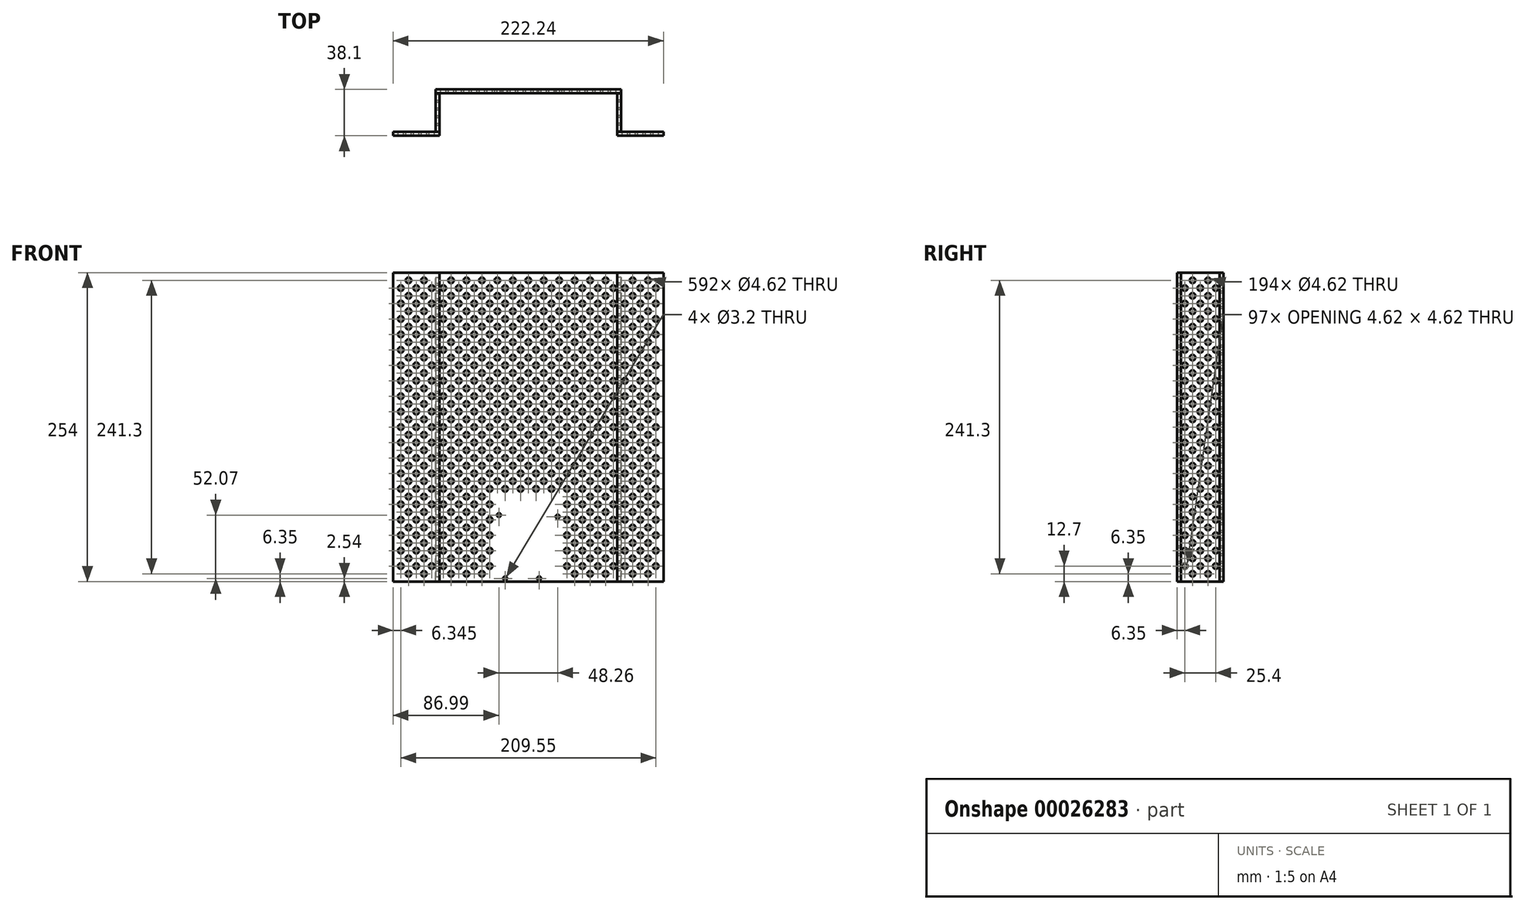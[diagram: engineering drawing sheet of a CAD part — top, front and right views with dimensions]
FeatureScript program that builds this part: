
annotation { "Feature Type Name" : "Feature", "Feature Type Description" : "" }
export const myFeature = defineFeature(function(context is Context, id is Id, definition is map)
    precondition{}
    {
        {
            var Q0;
            Q0=qCreatedBy(makeId("Front.planeOp"),FACE);
            var sketch = newSketch(context, id + "F0", { "sketchPlane" : qUnion([Q0])});
            skLineSegment(sketch, "E0.rect.bottom", {"start": v(76.2, -127) * mm, "end": v(-76.2, -127) * mm});
            skLineSegment(sketch, "E0.rect.top", {"start": v(76.2, 127) * mm, "end": v(-76.2, 127) * mm});
            skLineSegment(sketch, "E0.rect.left", {"start": v(76.2, -127) * mm, "end": v(76.2, 127) * mm});
            skLineSegment(sketch, "E0.rect.right", {"start": v(-76.2, -127) * mm, "end": v(-76.2, 127) * mm});
            skPoint(sketch, "E0.rect.middle", {"position": v(0, 0) * mm});
            skLineSegment(sketch, "E1", {"start": v(-76.2, -127) * mm, "end": v(-26.67, -127) * mm});
            skLineSegment(sketch, "E2", {"start": v(76.2, -127) * mm, "end": v(26.67, -127) * mm});
            skLineSegment(sketch, "E3.bottom", {"start": v(-26.67, -127) * mm, "end": v(26.67, -127) * mm});
            skLineSegment(sketch, "E3.top", {"start": v(-26.67, -58.42) * mm, "end": v(26.67, -58.42) * mm});
            skLineSegment(sketch, "E3.left", {"start": v(-26.67, -127) * mm, "end": v(-26.67, -58.42) * mm});
            skLineSegment(sketch, "E3.right", {"start": v(26.67, -127) * mm, "end": v(26.67, -58.42) * mm});
            skCircle(sketch, "E4", {"center": v(0, 120.65) * mm, "radius": 2.31 * mm});
            skCircle(sketch, "E5.0.1.0", {"center": v(0, 107.95) * mm, "radius": 2.31 * mm});
            skCircle(sketch, "E5.0.2.0", {"center": v(0, 95.25) * mm, "radius": 2.31 * mm});
            skCircle(sketch, "E5.0.3.0", {"center": v(0, 82.55) * mm, "radius": 2.31 * mm});
            skCircle(sketch, "E5.0.4.0", {"center": v(0, 69.85) * mm, "radius": 2.31 * mm});
            skCircle(sketch, "E5.0.5.0", {"center": v(0, 57.15) * mm, "radius": 2.31 * mm});
            skCircle(sketch, "E5.0.6.0", {"center": v(0, 44.45) * mm, "radius": 2.31 * mm});
            skCircle(sketch, "E5.0.7.0", {"center": v(0, 31.75) * mm, "radius": 2.31 * mm});
            skCircle(sketch, "E5.0.8.0", {"center": v(0, 19.05) * mm, "radius": 2.31 * mm});
            skCircle(sketch, "E5.0.9.0", {"center": v(0, 6.35) * mm, "radius": 2.31 * mm});
            skCircle(sketch, "E5.0.10.0", {"center": v(0, -6.35) * mm, "radius": 2.31 * mm});
            skCircle(sketch, "E5.0.11.0", {"center": v(0, -19.05) * mm, "radius": 2.31 * mm});
            skCircle(sketch, "E5.0.12.0", {"center": v(0, -31.75) * mm, "radius": 2.31 * mm});
            skCircle(sketch, "E5.0.13.0", {"center": v(0, -44.45) * mm, "radius": 2.31 * mm});
            skCircle(sketch, "E5.1.0.0", {"center": v(12.7, 120.65) * mm, "radius": 2.31 * mm});
            skCircle(sketch, "E5.1.1.0", {"center": v(12.7, 107.95) * mm, "radius": 2.31 * mm});
            skCircle(sketch, "E5.1.2.0", {"center": v(12.7, 95.25) * mm, "radius": 2.31 * mm});
            skCircle(sketch, "E5.1.3.0", {"center": v(12.7, 82.55) * mm, "radius": 2.31 * mm});
            skCircle(sketch, "E5.1.4.0", {"center": v(12.7, 69.85) * mm, "radius": 2.31 * mm});
            skCircle(sketch, "E5.1.5.0", {"center": v(12.7, 57.15) * mm, "radius": 2.31 * mm});
            skCircle(sketch, "E5.1.6.0", {"center": v(12.7, 44.45) * mm, "radius": 2.31 * mm});
            skCircle(sketch, "E5.1.7.0", {"center": v(12.7, 31.75) * mm, "radius": 2.31 * mm});
            skCircle(sketch, "E5.1.8.0", {"center": v(12.7, 19.05) * mm, "radius": 2.31 * mm});
            skCircle(sketch, "E5.1.9.0", {"center": v(12.7, 6.35) * mm, "radius": 2.31 * mm});
            skCircle(sketch, "E5.1.10.0", {"center": v(12.7, -6.35) * mm, "radius": 2.31 * mm});
            skCircle(sketch, "E5.1.11.0", {"center": v(12.7, -19.05) * mm, "radius": 2.31 * mm});
            skCircle(sketch, "E5.1.12.0", {"center": v(12.7, -31.75) * mm, "radius": 2.31 * mm});
            skCircle(sketch, "E5.1.13.0", {"center": v(12.7, -44.45) * mm, "radius": 2.31 * mm});
            skCircle(sketch, "E5.2.0.0", {"center": v(25.4, 120.65) * mm, "radius": 2.31 * mm});
            skCircle(sketch, "E5.2.1.0", {"center": v(25.4, 107.95) * mm, "radius": 2.31 * mm});
            skCircle(sketch, "E5.2.2.0", {"center": v(25.4, 95.25) * mm, "radius": 2.31 * mm});
            skCircle(sketch, "E5.2.3.0", {"center": v(25.4, 82.55) * mm, "radius": 2.31 * mm});
            skCircle(sketch, "E5.2.4.0", {"center": v(25.4, 69.85) * mm, "radius": 2.31 * mm});
            skCircle(sketch, "E5.2.5.0", {"center": v(25.4, 57.15) * mm, "radius": 2.31 * mm});
            skCircle(sketch, "E5.2.6.0", {"center": v(25.4, 44.45) * mm, "radius": 2.31 * mm});
            skCircle(sketch, "E5.2.7.0", {"center": v(25.4, 31.75) * mm, "radius": 2.31 * mm});
            skCircle(sketch, "E5.2.8.0", {"center": v(25.4, 19.05) * mm, "radius": 2.31 * mm});
            skCircle(sketch, "E5.2.9.0", {"center": v(25.4, 6.35) * mm, "radius": 2.31 * mm});
            skCircle(sketch, "E5.2.10.0", {"center": v(25.4, -6.35) * mm, "radius": 2.31 * mm});
            skCircle(sketch, "E5.2.11.0", {"center": v(25.4, -19.05) * mm, "radius": 2.31 * mm});
            skCircle(sketch, "E5.2.12.0", {"center": v(25.4, -31.75) * mm, "radius": 2.31 * mm});
            skCircle(sketch, "E5.2.13.0", {"center": v(25.4, -44.45) * mm, "radius": 2.31 * mm});
            skCircle(sketch, "E5.3.0.0", {"center": v(38.1, 120.65) * mm, "radius": 2.31 * mm});
            skCircle(sketch, "E5.3.1.0", {"center": v(38.1, 107.95) * mm, "radius": 2.31 * mm});
            skCircle(sketch, "E5.3.2.0", {"center": v(38.1, 95.25) * mm, "radius": 2.31 * mm});
            skCircle(sketch, "E5.3.3.0", {"center": v(38.1, 82.55) * mm, "radius": 2.31 * mm});
            skCircle(sketch, "E5.3.4.0", {"center": v(38.1, 69.85) * mm, "radius": 2.31 * mm});
            skCircle(sketch, "E5.3.5.0", {"center": v(38.1, 57.15) * mm, "radius": 2.31 * mm});
            skCircle(sketch, "E5.3.6.0", {"center": v(38.1, 44.45) * mm, "radius": 2.31 * mm});
            skCircle(sketch, "E5.3.7.0", {"center": v(38.1, 31.75) * mm, "radius": 2.31 * mm});
            skCircle(sketch, "E5.3.8.0", {"center": v(38.1, 19.05) * mm, "radius": 2.31 * mm});
            skCircle(sketch, "E5.3.9.0", {"center": v(38.1, 6.35) * mm, "radius": 2.31 * mm});
            skCircle(sketch, "E5.3.10.0", {"center": v(38.1, -6.35) * mm, "radius": 2.31 * mm});
            skCircle(sketch, "E5.3.11.0", {"center": v(38.1, -19.05) * mm, "radius": 2.31 * mm});
            skCircle(sketch, "E5.3.12.0", {"center": v(38.1, -31.75) * mm, "radius": 2.31 * mm});
            skCircle(sketch, "E5.3.13.0", {"center": v(38.1, -44.45) * mm, "radius": 2.31 * mm});
            skCircle(sketch, "E5.3.14.0", {"center": v(38.1, -57.15) * mm, "radius": 2.31 * mm});
            skCircle(sketch, "E5.3.15.0", {"center": v(38.1, -69.85) * mm, "radius": 2.31 * mm});
            skCircle(sketch, "E5.3.16.0", {"center": v(38.1, -82.55) * mm, "radius": 2.31 * mm});
            skCircle(sketch, "E5.3.17.0", {"center": v(38.1, -95.25) * mm, "radius": 2.31 * mm});
            skCircle(sketch, "E5.3.18.0", {"center": v(38.1, -107.95) * mm, "radius": 2.31 * mm});
            skCircle(sketch, "E5.3.19.0", {"center": v(38.1, -120.65) * mm, "radius": 2.31 * mm});
            skCircle(sketch, "E5.4.0.0", {"center": v(50.8, 120.65) * mm, "radius": 2.31 * mm});
            skCircle(sketch, "E5.4.1.0", {"center": v(50.8, 107.95) * mm, "radius": 2.31 * mm});
            skCircle(sketch, "E5.4.2.0", {"center": v(50.8, 95.25) * mm, "radius": 2.31 * mm});
            skCircle(sketch, "E5.4.3.0", {"center": v(50.8, 82.55) * mm, "radius": 2.31 * mm});
            skCircle(sketch, "E5.4.4.0", {"center": v(50.8, 69.85) * mm, "radius": 2.31 * mm});
            skCircle(sketch, "E5.4.5.0", {"center": v(50.8, 57.15) * mm, "radius": 2.31 * mm});
            skCircle(sketch, "E5.4.6.0", {"center": v(50.8, 44.45) * mm, "radius": 2.31 * mm});
            skCircle(sketch, "E5.4.7.0", {"center": v(50.8, 31.75) * mm, "radius": 2.31 * mm});
            skCircle(sketch, "E5.4.8.0", {"center": v(50.8, 19.05) * mm, "radius": 2.31 * mm});
            skCircle(sketch, "E5.4.9.0", {"center": v(50.8, 6.35) * mm, "radius": 2.31 * mm});
            skCircle(sketch, "E5.4.10.0", {"center": v(50.8, -6.35) * mm, "radius": 2.31 * mm});
            skCircle(sketch, "E5.4.11.0", {"center": v(50.8, -19.05) * mm, "radius": 2.31 * mm});
            skCircle(sketch, "E5.4.12.0", {"center": v(50.8, -31.75) * mm, "radius": 2.31 * mm});
            skCircle(sketch, "E5.4.13.0", {"center": v(50.8, -44.45) * mm, "radius": 2.31 * mm});
            skCircle(sketch, "E5.4.14.0", {"center": v(50.8, -57.15) * mm, "radius": 2.31 * mm});
            skCircle(sketch, "E5.4.15.0", {"center": v(50.8, -69.85) * mm, "radius": 2.31 * mm});
            skCircle(sketch, "E5.4.16.0", {"center": v(50.8, -82.55) * mm, "radius": 2.31 * mm});
            skCircle(sketch, "E5.4.17.0", {"center": v(50.8, -95.25) * mm, "radius": 2.31 * mm});
            skCircle(sketch, "E5.4.18.0", {"center": v(50.8, -107.95) * mm, "radius": 2.31 * mm});
            skCircle(sketch, "E5.4.19.0", {"center": v(50.8, -120.65) * mm, "radius": 2.31 * mm});
            skCircle(sketch, "E5.5.0.0", {"center": v(63.5, 120.65) * mm, "radius": 2.31 * mm});
            skCircle(sketch, "E5.5.1.0", {"center": v(63.5, 107.95) * mm, "radius": 2.31 * mm});
            skCircle(sketch, "E5.5.2.0", {"center": v(63.5, 95.25) * mm, "radius": 2.31 * mm});
            skCircle(sketch, "E5.5.3.0", {"center": v(63.5, 82.55) * mm, "radius": 2.31 * mm});
            skCircle(sketch, "E5.5.4.0", {"center": v(63.5, 69.85) * mm, "radius": 2.31 * mm});
            skCircle(sketch, "E5.5.5.0", {"center": v(63.5, 57.15) * mm, "radius": 2.31 * mm});
            skCircle(sketch, "E5.5.6.0", {"center": v(63.5, 44.45) * mm, "radius": 2.31 * mm});
            skCircle(sketch, "E5.5.7.0", {"center": v(63.5, 31.75) * mm, "radius": 2.31 * mm});
            skCircle(sketch, "E5.5.8.0", {"center": v(63.5, 19.05) * mm, "radius": 2.31 * mm});
            skCircle(sketch, "E5.5.9.0", {"center": v(63.5, 6.35) * mm, "radius": 2.31 * mm});
            skCircle(sketch, "E5.5.10.0", {"center": v(63.5, -6.35) * mm, "radius": 2.31 * mm});
            skCircle(sketch, "E5.5.11.0", {"center": v(63.5, -19.05) * mm, "radius": 2.31 * mm});
            skCircle(sketch, "E5.5.12.0", {"center": v(63.5, -31.75) * mm, "radius": 2.31 * mm});
            skCircle(sketch, "E5.5.13.0", {"center": v(63.5, -44.45) * mm, "radius": 2.31 * mm});
            skCircle(sketch, "E5.5.14.0", {"center": v(63.5, -57.15) * mm, "radius": 2.31 * mm});
            skCircle(sketch, "E5.5.15.0", {"center": v(63.5, -69.85) * mm, "radius": 2.31 * mm});
            skCircle(sketch, "E5.5.16.0", {"center": v(63.5, -82.55) * mm, "radius": 2.31 * mm});
            skCircle(sketch, "E5.5.17.0", {"center": v(63.5, -95.25) * mm, "radius": 2.31 * mm});
            skCircle(sketch, "E5.5.18.0", {"center": v(63.5, -107.95) * mm, "radius": 2.31 * mm});
            skCircle(sketch, "E5.5.19.0", {"center": v(63.5, -120.65) * mm, "radius": 2.31 * mm});
            skLineSegment(sketch, "E5.direction1", {"start": v(0, 120.65) * mm, "end": v(12.7, 120.65) * mm, "construction": true});
            skLineSegment(sketch, "E5.direction2", {"start": v(0, 120.65) * mm, "end": v(0, 107.95) * mm, "construction": true});
            skCircle(sketch, "E6", {"center": v(-12.7, 120.65) * mm, "radius": 2.31 * mm});
            skCircle(sketch, "E7.0.1.0", {"center": v(-12.7, 107.95) * mm, "radius": 2.31 * mm});
            skCircle(sketch, "E7.0.2.0", {"center": v(-12.7, 95.25) * mm, "radius": 2.31 * mm});
            skCircle(sketch, "E7.0.3.0", {"center": v(-12.7, 82.55) * mm, "radius": 2.31 * mm});
            skCircle(sketch, "E7.0.4.0", {"center": v(-12.7, 69.85) * mm, "radius": 2.31 * mm});
            skCircle(sketch, "E7.0.5.0", {"center": v(-12.7, 57.15) * mm, "radius": 2.31 * mm});
            skCircle(sketch, "E7.0.6.0", {"center": v(-12.7, 44.45) * mm, "radius": 2.31 * mm});
            skCircle(sketch, "E7.0.7.0", {"center": v(-12.7, 31.75) * mm, "radius": 2.31 * mm});
            skCircle(sketch, "E7.0.8.0", {"center": v(-12.7, 19.05) * mm, "radius": 2.31 * mm});
            skCircle(sketch, "E7.0.9.0", {"center": v(-12.7, 6.35) * mm, "radius": 2.31 * mm});
            skCircle(sketch, "E7.0.10.0", {"center": v(-12.7, -6.35) * mm, "radius": 2.31 * mm});
            skCircle(sketch, "E7.0.11.0", {"center": v(-12.7, -19.05) * mm, "radius": 2.31 * mm});
            skCircle(sketch, "E7.0.12.0", {"center": v(-12.7, -31.75) * mm, "radius": 2.31 * mm});
            skCircle(sketch, "E7.0.13.0", {"center": v(-12.7, -44.45) * mm, "radius": 2.31 * mm});
            skCircle(sketch, "E7.1.0.0", {"center": v(-25.4, 120.65) * mm, "radius": 2.31 * mm});
            skCircle(sketch, "E7.1.1.0", {"center": v(-25.4, 107.95) * mm, "radius": 2.31 * mm});
            skCircle(sketch, "E7.1.2.0", {"center": v(-25.4, 95.25) * mm, "radius": 2.31 * mm});
            skCircle(sketch, "E7.1.3.0", {"center": v(-25.4, 82.55) * mm, "radius": 2.31 * mm});
            skCircle(sketch, "E7.1.4.0", {"center": v(-25.4, 69.85) * mm, "radius": 2.31 * mm});
            skCircle(sketch, "E7.1.5.0", {"center": v(-25.4, 57.15) * mm, "radius": 2.31 * mm});
            skCircle(sketch, "E7.1.6.0", {"center": v(-25.4, 44.45) * mm, "radius": 2.31 * mm});
            skCircle(sketch, "E7.1.7.0", {"center": v(-25.4, 31.75) * mm, "radius": 2.31 * mm});
            skCircle(sketch, "E7.1.8.0", {"center": v(-25.4, 19.05) * mm, "radius": 2.31 * mm});
            skCircle(sketch, "E7.1.9.0", {"center": v(-25.4, 6.35) * mm, "radius": 2.31 * mm});
            skCircle(sketch, "E7.1.10.0", {"center": v(-25.4, -6.35) * mm, "radius": 2.31 * mm});
            skCircle(sketch, "E7.1.11.0", {"center": v(-25.4, -19.05) * mm, "radius": 2.31 * mm});
            skCircle(sketch, "E7.1.12.0", {"center": v(-25.4, -31.75) * mm, "radius": 2.31 * mm});
            skCircle(sketch, "E7.1.13.0", {"center": v(-25.4, -44.45) * mm, "radius": 2.31 * mm});
            skCircle(sketch, "E7.2.0.0", {"center": v(-38.1, 120.65) * mm, "radius": 2.31 * mm});
            skCircle(sketch, "E7.2.1.0", {"center": v(-38.1, 107.95) * mm, "radius": 2.31 * mm});
            skCircle(sketch, "E7.2.2.0", {"center": v(-38.1, 95.25) * mm, "radius": 2.31 * mm});
            skCircle(sketch, "E7.2.3.0", {"center": v(-38.1, 82.55) * mm, "radius": 2.31 * mm});
            skCircle(sketch, "E7.2.4.0", {"center": v(-38.1, 69.85) * mm, "radius": 2.31 * mm});
            skCircle(sketch, "E7.2.5.0", {"center": v(-38.1, 57.15) * mm, "radius": 2.31 * mm});
            skCircle(sketch, "E7.2.6.0", {"center": v(-38.1, 44.45) * mm, "radius": 2.31 * mm});
            skCircle(sketch, "E7.2.7.0", {"center": v(-38.1, 31.75) * mm, "radius": 2.31 * mm});
            skCircle(sketch, "E7.2.8.0", {"center": v(-38.1, 19.05) * mm, "radius": 2.31 * mm});
            skCircle(sketch, "E7.2.9.0", {"center": v(-38.1, 6.35) * mm, "radius": 2.31 * mm});
            skCircle(sketch, "E7.2.10.0", {"center": v(-38.1, -6.35) * mm, "radius": 2.31 * mm});
            skCircle(sketch, "E7.2.11.0", {"center": v(-38.1, -19.05) * mm, "radius": 2.31 * mm});
            skCircle(sketch, "E7.2.12.0", {"center": v(-38.1, -31.75) * mm, "radius": 2.31 * mm});
            skCircle(sketch, "E7.2.13.0", {"center": v(-38.1, -44.45) * mm, "radius": 2.31 * mm});
            skCircle(sketch, "E7.2.14.0", {"center": v(-38.1, -57.15) * mm, "radius": 2.31 * mm});
            skCircle(sketch, "E7.2.15.0", {"center": v(-38.1, -69.85) * mm, "radius": 2.31 * mm});
            skCircle(sketch, "E7.2.16.0", {"center": v(-38.1, -82.55) * mm, "radius": 2.31 * mm});
            skCircle(sketch, "E7.2.17.0", {"center": v(-38.1, -95.25) * mm, "radius": 2.31 * mm});
            skCircle(sketch, "E7.2.18.0", {"center": v(-38.1, -107.95) * mm, "radius": 2.31 * mm});
            skCircle(sketch, "E7.2.19.0", {"center": v(-38.1, -120.65) * mm, "radius": 2.31 * mm});
            skCircle(sketch, "E7.3.0.0", {"center": v(-50.8, 120.65) * mm, "radius": 2.31 * mm});
            skCircle(sketch, "E7.3.1.0", {"center": v(-50.8, 107.95) * mm, "radius": 2.31 * mm});
            skCircle(sketch, "E7.3.2.0", {"center": v(-50.8, 95.25) * mm, "radius": 2.31 * mm});
            skCircle(sketch, "E7.3.3.0", {"center": v(-50.8, 82.55) * mm, "radius": 2.31 * mm});
            skCircle(sketch, "E7.3.4.0", {"center": v(-50.8, 69.85) * mm, "radius": 2.31 * mm});
            skCircle(sketch, "E7.3.5.0", {"center": v(-50.8, 57.15) * mm, "radius": 2.31 * mm});
            skCircle(sketch, "E7.3.6.0", {"center": v(-50.8, 44.45) * mm, "radius": 2.31 * mm});
            skCircle(sketch, "E7.3.7.0", {"center": v(-50.8, 31.75) * mm, "radius": 2.31 * mm});
            skCircle(sketch, "E7.3.8.0", {"center": v(-50.8, 19.05) * mm, "radius": 2.31 * mm});
            skCircle(sketch, "E7.3.9.0", {"center": v(-50.8, 6.35) * mm, "radius": 2.31 * mm});
            skCircle(sketch, "E7.3.10.0", {"center": v(-50.8, -6.35) * mm, "radius": 2.31 * mm});
            skCircle(sketch, "E7.3.11.0", {"center": v(-50.8, -19.05) * mm, "radius": 2.31 * mm});
            skCircle(sketch, "E7.3.12.0", {"center": v(-50.8, -31.75) * mm, "radius": 2.31 * mm});
            skCircle(sketch, "E7.3.13.0", {"center": v(-50.8, -44.45) * mm, "radius": 2.31 * mm});
            skCircle(sketch, "E7.3.14.0", {"center": v(-50.8, -57.15) * mm, "radius": 2.31 * mm});
            skCircle(sketch, "E7.3.15.0", {"center": v(-50.8, -69.85) * mm, "radius": 2.31 * mm});
            skCircle(sketch, "E7.3.16.0", {"center": v(-50.8, -82.55) * mm, "radius": 2.31 * mm});
            skCircle(sketch, "E7.3.17.0", {"center": v(-50.8, -95.25) * mm, "radius": 2.31 * mm});
            skCircle(sketch, "E7.3.18.0", {"center": v(-50.8, -107.95) * mm, "radius": 2.31 * mm});
            skCircle(sketch, "E7.3.19.0", {"center": v(-50.8, -120.65) * mm, "radius": 2.31 * mm});
            skCircle(sketch, "E7.4.0.0", {"center": v(-63.5, 120.65) * mm, "radius": 2.31 * mm});
            skCircle(sketch, "E7.4.1.0", {"center": v(-63.5, 107.95) * mm, "radius": 2.31 * mm});
            skCircle(sketch, "E7.4.2.0", {"center": v(-63.5, 95.25) * mm, "radius": 2.31 * mm});
            skCircle(sketch, "E7.4.3.0", {"center": v(-63.5, 82.55) * mm, "radius": 2.31 * mm});
            skCircle(sketch, "E7.4.4.0", {"center": v(-63.5, 69.85) * mm, "radius": 2.31 * mm});
            skCircle(sketch, "E7.4.5.0", {"center": v(-63.5, 57.15) * mm, "radius": 2.31 * mm});
            skCircle(sketch, "E7.4.6.0", {"center": v(-63.5, 44.45) * mm, "radius": 2.31 * mm});
            skCircle(sketch, "E7.4.7.0", {"center": v(-63.5, 31.75) * mm, "radius": 2.31 * mm});
            skCircle(sketch, "E7.4.8.0", {"center": v(-63.5, 19.05) * mm, "radius": 2.31 * mm});
            skCircle(sketch, "E7.4.9.0", {"center": v(-63.5, 6.35) * mm, "radius": 2.31 * mm});
            skCircle(sketch, "E7.4.10.0", {"center": v(-63.5, -6.35) * mm, "radius": 2.31 * mm});
            skCircle(sketch, "E7.4.11.0", {"center": v(-63.5, -19.05) * mm, "radius": 2.31 * mm});
            skCircle(sketch, "E7.4.12.0", {"center": v(-63.5, -31.75) * mm, "radius": 2.31 * mm});
            skCircle(sketch, "E7.4.13.0", {"center": v(-63.5, -44.45) * mm, "radius": 2.31 * mm});
            skCircle(sketch, "E7.4.14.0", {"center": v(-63.5, -57.15) * mm, "radius": 2.31 * mm});
            skCircle(sketch, "E7.4.15.0", {"center": v(-63.5, -69.85) * mm, "radius": 2.31 * mm});
            skCircle(sketch, "E7.4.16.0", {"center": v(-63.5, -82.55) * mm, "radius": 2.31 * mm});
            skCircle(sketch, "E7.4.17.0", {"center": v(-63.5, -95.25) * mm, "radius": 2.31 * mm});
            skCircle(sketch, "E7.4.18.0", {"center": v(-63.5, -107.95) * mm, "radius": 2.31 * mm});
            skCircle(sketch, "E7.4.19.0", {"center": v(-63.5, -120.65) * mm, "radius": 2.31 * mm});
            skLineSegment(sketch, "E7.direction1", {"start": v(-12.7, 120.65) * mm, "end": v(-25.4, 120.65) * mm, "construction": true});
            skLineSegment(sketch, "E7.direction2", {"start": v(-12.7, 120.65) * mm, "end": v(-12.7, 107.95) * mm, "construction": true});
            skCircle(sketch, "E8", {"center": v(6.35, 114.3) * mm, "radius": 2.31 * mm});
            skCircle(sketch, "E9.0.1.0", {"center": v(6.35, 101.6) * mm, "radius": 2.31 * mm});
            skCircle(sketch, "E9.0.2.0", {"center": v(6.35, 88.9) * mm, "radius": 2.31 * mm});
            skCircle(sketch, "E9.0.3.0", {"center": v(6.35, 76.2) * mm, "radius": 2.31 * mm});
            skCircle(sketch, "E9.0.4.0", {"center": v(6.35, 63.5) * mm, "radius": 2.31 * mm});
            skCircle(sketch, "E9.0.5.0", {"center": v(6.35, 50.8) * mm, "radius": 2.31 * mm});
            skCircle(sketch, "E9.0.6.0", {"center": v(6.35, 38.1) * mm, "radius": 2.31 * mm});
            skCircle(sketch, "E9.0.7.0", {"center": v(6.35, 25.4) * mm, "radius": 2.31 * mm});
            skCircle(sketch, "E9.0.8.0", {"center": v(6.35, 12.7) * mm, "radius": 2.31 * mm});
            skCircle(sketch, "E9.0.9.0", {"center": v(6.35, 0) * mm, "radius": 2.31 * mm});
            skCircle(sketch, "E9.0.10.0", {"center": v(6.35, -12.7) * mm, "radius": 2.31 * mm});
            skCircle(sketch, "E9.0.11.0", {"center": v(6.35, -25.4) * mm, "radius": 2.31 * mm});
            skCircle(sketch, "E9.0.12.0", {"center": v(6.35, -38.1) * mm, "radius": 2.31 * mm});
            skCircle(sketch, "E9.0.13.0", {"center": v(6.35, -50.8) * mm, "radius": 2.31 * mm});
            skCircle(sketch, "E9.1.0.0", {"center": v(19.05, 114.3) * mm, "radius": 2.31 * mm});
            skCircle(sketch, "E9.1.1.0", {"center": v(19.05, 101.6) * mm, "radius": 2.31 * mm});
            skCircle(sketch, "E9.1.2.0", {"center": v(19.05, 88.9) * mm, "radius": 2.31 * mm});
            skCircle(sketch, "E9.1.3.0", {"center": v(19.05, 76.2) * mm, "radius": 2.31 * mm});
            skCircle(sketch, "E9.1.4.0", {"center": v(19.05, 63.5) * mm, "radius": 2.31 * mm});
            skCircle(sketch, "E9.1.5.0", {"center": v(19.05, 50.8) * mm, "radius": 2.31 * mm});
            skCircle(sketch, "E9.1.6.0", {"center": v(19.05, 38.1) * mm, "radius": 2.31 * mm});
            skCircle(sketch, "E9.1.7.0", {"center": v(19.05, 25.4) * mm, "radius": 2.31 * mm});
            skCircle(sketch, "E9.1.8.0", {"center": v(19.05, 12.7) * mm, "radius": 2.31 * mm});
            skCircle(sketch, "E9.1.9.0", {"center": v(19.05, 0) * mm, "radius": 2.31 * mm});
            skCircle(sketch, "E9.1.10.0", {"center": v(19.05, -12.7) * mm, "radius": 2.31 * mm});
            skCircle(sketch, "E9.1.11.0", {"center": v(19.05, -25.4) * mm, "radius": 2.31 * mm});
            skCircle(sketch, "E9.1.12.0", {"center": v(19.05, -38.1) * mm, "radius": 2.31 * mm});
            skCircle(sketch, "E9.1.13.0", {"center": v(19.05, -50.8) * mm, "radius": 2.31 * mm});
            skCircle(sketch, "E9.2.0.0", {"center": v(31.75, 114.3) * mm, "radius": 2.31 * mm});
            skCircle(sketch, "E9.2.1.0", {"center": v(31.75, 101.6) * mm, "radius": 2.31 * mm});
            skCircle(sketch, "E9.2.2.0", {"center": v(31.75, 88.9) * mm, "radius": 2.31 * mm});
            skCircle(sketch, "E9.2.3.0", {"center": v(31.75, 76.2) * mm, "radius": 2.31 * mm});
            skCircle(sketch, "E9.2.4.0", {"center": v(31.75, 63.5) * mm, "radius": 2.31 * mm});
            skCircle(sketch, "E9.2.5.0", {"center": v(31.75, 50.8) * mm, "radius": 2.31 * mm});
            skCircle(sketch, "E9.2.6.0", {"center": v(31.75, 38.1) * mm, "radius": 2.31 * mm});
            skCircle(sketch, "E9.2.7.0", {"center": v(31.75, 25.4) * mm, "radius": 2.31 * mm});
            skCircle(sketch, "E9.2.8.0", {"center": v(31.75, 12.7) * mm, "radius": 2.31 * mm});
            skCircle(sketch, "E9.2.9.0", {"center": v(31.75, 0) * mm, "radius": 2.31 * mm});
            skCircle(sketch, "E9.2.10.0", {"center": v(31.75, -12.7) * mm, "radius": 2.31 * mm});
            skCircle(sketch, "E9.2.11.0", {"center": v(31.75, -25.4) * mm, "radius": 2.31 * mm});
            skCircle(sketch, "E9.2.12.0", {"center": v(31.75, -38.1) * mm, "radius": 2.31 * mm});
            skCircle(sketch, "E9.2.13.0", {"center": v(31.75, -50.8) * mm, "radius": 2.31 * mm});
            skCircle(sketch, "E9.2.14.0", {"center": v(31.75, -63.5) * mm, "radius": 2.31 * mm});
            skCircle(sketch, "E9.2.15.0", {"center": v(31.75, -76.2) * mm, "radius": 2.31 * mm});
            skCircle(sketch, "E9.2.16.0", {"center": v(31.75, -88.9) * mm, "radius": 2.31 * mm});
            skCircle(sketch, "E9.2.17.0", {"center": v(31.75, -101.6) * mm, "radius": 2.31 * mm});
            skCircle(sketch, "E9.2.18.0", {"center": v(31.75, -114.3) * mm, "radius": 2.31 * mm});
            skCircle(sketch, "E9.3.0.0", {"center": v(44.45, 114.3) * mm, "radius": 2.31 * mm});
            skCircle(sketch, "E9.3.1.0", {"center": v(44.45, 101.6) * mm, "radius": 2.31 * mm});
            skCircle(sketch, "E9.3.2.0", {"center": v(44.45, 88.9) * mm, "radius": 2.31 * mm});
            skCircle(sketch, "E9.3.3.0", {"center": v(44.45, 76.2) * mm, "radius": 2.31 * mm});
            skCircle(sketch, "E9.3.4.0", {"center": v(44.45, 63.5) * mm, "radius": 2.31 * mm});
            skCircle(sketch, "E9.3.5.0", {"center": v(44.45, 50.8) * mm, "radius": 2.31 * mm});
            skCircle(sketch, "E9.3.6.0", {"center": v(44.45, 38.1) * mm, "radius": 2.31 * mm});
            skCircle(sketch, "E9.3.7.0", {"center": v(44.45, 25.4) * mm, "radius": 2.31 * mm});
            skCircle(sketch, "E9.3.8.0", {"center": v(44.45, 12.7) * mm, "radius": 2.31 * mm});
            skCircle(sketch, "E9.3.9.0", {"center": v(44.45, 0) * mm, "radius": 2.31 * mm});
            skCircle(sketch, "E9.3.10.0", {"center": v(44.45, -12.7) * mm, "radius": 2.31 * mm});
            skCircle(sketch, "E9.3.11.0", {"center": v(44.45, -25.4) * mm, "radius": 2.31 * mm});
            skCircle(sketch, "E9.3.12.0", {"center": v(44.45, -38.1) * mm, "radius": 2.31 * mm});
            skCircle(sketch, "E9.3.13.0", {"center": v(44.45, -50.8) * mm, "radius": 2.31 * mm});
            skCircle(sketch, "E9.3.14.0", {"center": v(44.45, -63.5) * mm, "radius": 2.31 * mm});
            skCircle(sketch, "E9.3.15.0", {"center": v(44.45, -76.2) * mm, "radius": 2.31 * mm});
            skCircle(sketch, "E9.3.16.0", {"center": v(44.45, -88.9) * mm, "radius": 2.31 * mm});
            skCircle(sketch, "E9.3.17.0", {"center": v(44.45, -101.6) * mm, "radius": 2.31 * mm});
            skCircle(sketch, "E9.3.18.0", {"center": v(44.45, -114.3) * mm, "radius": 2.31 * mm});
            skCircle(sketch, "E9.4.0.0", {"center": v(57.15, 114.3) * mm, "radius": 2.31 * mm});
            skCircle(sketch, "E9.4.1.0", {"center": v(57.15, 101.6) * mm, "radius": 2.31 * mm});
            skCircle(sketch, "E9.4.2.0", {"center": v(57.15, 88.9) * mm, "radius": 2.31 * mm});
            skCircle(sketch, "E9.4.3.0", {"center": v(57.15, 76.2) * mm, "radius": 2.31 * mm});
            skCircle(sketch, "E9.4.4.0", {"center": v(57.15, 63.5) * mm, "radius": 2.31 * mm});
            skCircle(sketch, "E9.4.5.0", {"center": v(57.15, 50.8) * mm, "radius": 2.31 * mm});
            skCircle(sketch, "E9.4.6.0", {"center": v(57.15, 38.1) * mm, "radius": 2.31 * mm});
            skCircle(sketch, "E9.4.7.0", {"center": v(57.15, 25.4) * mm, "radius": 2.31 * mm});
            skCircle(sketch, "E9.4.8.0", {"center": v(57.15, 12.7) * mm, "radius": 2.31 * mm});
            skCircle(sketch, "E9.4.9.0", {"center": v(57.15, 0) * mm, "radius": 2.31 * mm});
            skCircle(sketch, "E9.4.10.0", {"center": v(57.15, -12.7) * mm, "radius": 2.31 * mm});
            skCircle(sketch, "E9.4.11.0", {"center": v(57.15, -25.4) * mm, "radius": 2.31 * mm});
            skCircle(sketch, "E9.4.12.0", {"center": v(57.15, -38.1) * mm, "radius": 2.31 * mm});
            skCircle(sketch, "E9.4.13.0", {"center": v(57.15, -50.8) * mm, "radius": 2.31 * mm});
            skCircle(sketch, "E9.4.14.0", {"center": v(57.15, -63.5) * mm, "radius": 2.31 * mm});
            skCircle(sketch, "E9.4.15.0", {"center": v(57.15, -76.2) * mm, "radius": 2.31 * mm});
            skCircle(sketch, "E9.4.16.0", {"center": v(57.15, -88.9) * mm, "radius": 2.31 * mm});
            skCircle(sketch, "E9.4.17.0", {"center": v(57.15, -101.6) * mm, "radius": 2.31 * mm});
            skCircle(sketch, "E9.4.18.0", {"center": v(57.15, -114.3) * mm, "radius": 2.31 * mm});
            skCircle(sketch, "E9.5.0.0", {"center": v(69.85, 114.3) * mm, "radius": 2.31 * mm});
            skCircle(sketch, "E9.5.1.0", {"center": v(69.85, 101.6) * mm, "radius": 2.31 * mm});
            skCircle(sketch, "E9.5.2.0", {"center": v(69.85, 88.9) * mm, "radius": 2.31 * mm});
            skCircle(sketch, "E9.5.3.0", {"center": v(69.85, 76.2) * mm, "radius": 2.31 * mm});
            skCircle(sketch, "E9.5.4.0", {"center": v(69.85, 63.5) * mm, "radius": 2.31 * mm});
            skCircle(sketch, "E9.5.5.0", {"center": v(69.85, 50.8) * mm, "radius": 2.31 * mm});
            skCircle(sketch, "E9.5.6.0", {"center": v(69.85, 38.1) * mm, "radius": 2.31 * mm});
            skCircle(sketch, "E9.5.7.0", {"center": v(69.85, 25.4) * mm, "radius": 2.31 * mm});
            skCircle(sketch, "E9.5.8.0", {"center": v(69.85, 12.7) * mm, "radius": 2.31 * mm});
            skCircle(sketch, "E9.5.9.0", {"center": v(69.85, 0) * mm, "radius": 2.31 * mm});
            skCircle(sketch, "E9.5.10.0", {"center": v(69.85, -12.7) * mm, "radius": 2.31 * mm});
            skCircle(sketch, "E9.5.11.0", {"center": v(69.85, -25.4) * mm, "radius": 2.31 * mm});
            skCircle(sketch, "E9.5.12.0", {"center": v(69.85, -38.1) * mm, "radius": 2.31 * mm});
            skCircle(sketch, "E9.5.13.0", {"center": v(69.85, -50.8) * mm, "radius": 2.31 * mm});
            skCircle(sketch, "E9.5.14.0", {"center": v(69.85, -63.5) * mm, "radius": 2.31 * mm});
            skCircle(sketch, "E9.5.15.0", {"center": v(69.85, -76.2) * mm, "radius": 2.31 * mm});
            skCircle(sketch, "E9.5.16.0", {"center": v(69.85, -88.9) * mm, "radius": 2.31 * mm});
            skCircle(sketch, "E9.5.17.0", {"center": v(69.85, -101.6) * mm, "radius": 2.31 * mm});
            skCircle(sketch, "E9.5.18.0", {"center": v(69.85, -114.3) * mm, "radius": 2.31 * mm});
            skLineSegment(sketch, "E9.direction1", {"start": v(6.35, 114.3) * mm, "end": v(19.05, 114.3) * mm, "construction": true});
            skLineSegment(sketch, "E9.direction2", {"start": v(6.35, 114.3) * mm, "end": v(6.35, 101.6) * mm, "construction": true});
            skCircle(sketch, "E10", {"center": v(-6.35, 114.3) * mm, "radius": 2.31 * mm});
            skCircle(sketch, "E11.0.1.0", {"center": v(-6.35, 101.6) * mm, "radius": 2.31 * mm});
            skCircle(sketch, "E11.0.2.0", {"center": v(-6.35, 88.9) * mm, "radius": 2.31 * mm});
            skCircle(sketch, "E11.0.3.0", {"center": v(-6.35, 76.2) * mm, "radius": 2.31 * mm});
            skCircle(sketch, "E11.0.4.0", {"center": v(-6.35, 63.5) * mm, "radius": 2.31 * mm});
            skCircle(sketch, "E11.0.5.0", {"center": v(-6.35, 50.8) * mm, "radius": 2.31 * mm});
            skCircle(sketch, "E11.0.6.0", {"center": v(-6.35, 38.1) * mm, "radius": 2.31 * mm});
            skCircle(sketch, "E11.0.7.0", {"center": v(-6.35, 25.4) * mm, "radius": 2.31 * mm});
            skCircle(sketch, "E11.0.8.0", {"center": v(-6.35, 12.7) * mm, "radius": 2.31 * mm});
            skCircle(sketch, "E11.0.9.0", {"center": v(-6.35, 0) * mm, "radius": 2.31 * mm});
            skCircle(sketch, "E11.0.10.0", {"center": v(-6.35, -12.7) * mm, "radius": 2.31 * mm});
            skCircle(sketch, "E11.0.11.0", {"center": v(-6.35, -25.4) * mm, "radius": 2.31 * mm});
            skCircle(sketch, "E11.0.12.0", {"center": v(-6.35, -38.1) * mm, "radius": 2.31 * mm});
            skCircle(sketch, "E11.0.13.0", {"center": v(-6.35, -50.8) * mm, "radius": 2.31 * mm});
            skCircle(sketch, "E11.1.0.0", {"center": v(-19.05, 114.3) * mm, "radius": 2.31 * mm});
            skCircle(sketch, "E11.1.1.0", {"center": v(-19.05, 101.6) * mm, "radius": 2.31 * mm});
            skCircle(sketch, "E11.1.2.0", {"center": v(-19.05, 88.9) * mm, "radius": 2.31 * mm});
            skCircle(sketch, "E11.1.3.0", {"center": v(-19.05, 76.2) * mm, "radius": 2.31 * mm});
            skCircle(sketch, "E11.1.4.0", {"center": v(-19.05, 63.5) * mm, "radius": 2.31 * mm});
            skCircle(sketch, "E11.1.5.0", {"center": v(-19.05, 50.8) * mm, "radius": 2.31 * mm});
            skCircle(sketch, "E11.1.6.0", {"center": v(-19.05, 38.1) * mm, "radius": 2.31 * mm});
            skCircle(sketch, "E11.1.7.0", {"center": v(-19.05, 25.4) * mm, "radius": 2.31 * mm});
            skCircle(sketch, "E11.1.8.0", {"center": v(-19.05, 12.7) * mm, "radius": 2.31 * mm});
            skCircle(sketch, "E11.1.9.0", {"center": v(-19.05, 0) * mm, "radius": 2.31 * mm});
            skCircle(sketch, "E11.1.10.0", {"center": v(-19.05, -12.7) * mm, "radius": 2.31 * mm});
            skCircle(sketch, "E11.1.11.0", {"center": v(-19.05, -25.4) * mm, "radius": 2.31 * mm});
            skCircle(sketch, "E11.1.12.0", {"center": v(-19.05, -38.1) * mm, "radius": 2.31 * mm});
            skCircle(sketch, "E11.1.13.0", {"center": v(-19.05, -50.8) * mm, "radius": 2.31 * mm});
            skCircle(sketch, "E11.2.0.0", {"center": v(-31.75, 114.3) * mm, "radius": 2.31 * mm});
            skCircle(sketch, "E11.2.1.0", {"center": v(-31.75, 101.6) * mm, "radius": 2.31 * mm});
            skCircle(sketch, "E11.2.2.0", {"center": v(-31.75, 88.9) * mm, "radius": 2.31 * mm});
            skCircle(sketch, "E11.2.3.0", {"center": v(-31.75, 76.2) * mm, "radius": 2.31 * mm});
            skCircle(sketch, "E11.2.4.0", {"center": v(-31.75, 63.5) * mm, "radius": 2.31 * mm});
            skCircle(sketch, "E11.2.5.0", {"center": v(-31.75, 50.8) * mm, "radius": 2.31 * mm});
            skCircle(sketch, "E11.2.6.0", {"center": v(-31.75, 38.1) * mm, "radius": 2.31 * mm});
            skCircle(sketch, "E11.2.7.0", {"center": v(-31.75, 25.4) * mm, "radius": 2.31 * mm});
            skCircle(sketch, "E11.2.8.0", {"center": v(-31.75, 12.7) * mm, "radius": 2.31 * mm});
            skCircle(sketch, "E11.2.9.0", {"center": v(-31.75, 0) * mm, "radius": 2.31 * mm});
            skCircle(sketch, "E11.2.10.0", {"center": v(-31.75, -12.7) * mm, "radius": 2.31 * mm});
            skCircle(sketch, "E11.2.11.0", {"center": v(-31.75, -25.4) * mm, "radius": 2.31 * mm});
            skCircle(sketch, "E11.2.12.0", {"center": v(-31.75, -38.1) * mm, "radius": 2.31 * mm});
            skCircle(sketch, "E11.2.13.0", {"center": v(-31.75, -50.8) * mm, "radius": 2.31 * mm});
            skCircle(sketch, "E11.2.14.0", {"center": v(-31.75, -63.5) * mm, "radius": 2.31 * mm});
            skCircle(sketch, "E11.2.15.0", {"center": v(-31.75, -76.2) * mm, "radius": 2.31 * mm});
            skCircle(sketch, "E11.2.16.0", {"center": v(-31.75, -88.9) * mm, "radius": 2.31 * mm});
            skCircle(sketch, "E11.2.17.0", {"center": v(-31.75, -101.6) * mm, "radius": 2.31 * mm});
            skCircle(sketch, "E11.2.18.0", {"center": v(-31.75, -114.3) * mm, "radius": 2.31 * mm});
            skCircle(sketch, "E11.3.0.0", {"center": v(-44.45, 114.3) * mm, "radius": 2.31 * mm});
            skCircle(sketch, "E11.3.1.0", {"center": v(-44.45, 101.6) * mm, "radius": 2.31 * mm});
            skCircle(sketch, "E11.3.2.0", {"center": v(-44.45, 88.9) * mm, "radius": 2.31 * mm});
            skCircle(sketch, "E11.3.3.0", {"center": v(-44.45, 76.2) * mm, "radius": 2.31 * mm});
            skCircle(sketch, "E11.3.4.0", {"center": v(-44.45, 63.5) * mm, "radius": 2.31 * mm});
            skCircle(sketch, "E11.3.5.0", {"center": v(-44.45, 50.8) * mm, "radius": 2.31 * mm});
            skCircle(sketch, "E11.3.6.0", {"center": v(-44.45, 38.1) * mm, "radius": 2.31 * mm});
            skCircle(sketch, "E11.3.7.0", {"center": v(-44.45, 25.4) * mm, "radius": 2.31 * mm});
            skCircle(sketch, "E11.3.8.0", {"center": v(-44.45, 12.7) * mm, "radius": 2.31 * mm});
            skCircle(sketch, "E11.3.9.0", {"center": v(-44.45, 0) * mm, "radius": 2.31 * mm});
            skCircle(sketch, "E11.3.10.0", {"center": v(-44.45, -12.7) * mm, "radius": 2.31 * mm});
            skCircle(sketch, "E11.3.11.0", {"center": v(-44.45, -25.4) * mm, "radius": 2.31 * mm});
            skCircle(sketch, "E11.3.12.0", {"center": v(-44.45, -38.1) * mm, "radius": 2.31 * mm});
            skCircle(sketch, "E11.3.13.0", {"center": v(-44.45, -50.8) * mm, "radius": 2.31 * mm});
            skCircle(sketch, "E11.3.14.0", {"center": v(-44.45, -63.5) * mm, "radius": 2.31 * mm});
            skCircle(sketch, "E11.3.15.0", {"center": v(-44.45, -76.2) * mm, "radius": 2.31 * mm});
            skCircle(sketch, "E11.3.16.0", {"center": v(-44.45, -88.9) * mm, "radius": 2.31 * mm});
            skCircle(sketch, "E11.3.17.0", {"center": v(-44.45, -101.6) * mm, "radius": 2.31 * mm});
            skCircle(sketch, "E11.3.18.0", {"center": v(-44.45, -114.3) * mm, "radius": 2.31 * mm});
            skCircle(sketch, "E11.4.0.0", {"center": v(-57.15, 114.3) * mm, "radius": 2.31 * mm});
            skCircle(sketch, "E11.4.1.0", {"center": v(-57.15, 101.6) * mm, "radius": 2.31 * mm});
            skCircle(sketch, "E11.4.2.0", {"center": v(-57.15, 88.9) * mm, "radius": 2.31 * mm});
            skCircle(sketch, "E11.4.3.0", {"center": v(-57.15, 76.2) * mm, "radius": 2.31 * mm});
            skCircle(sketch, "E11.4.4.0", {"center": v(-57.15, 63.5) * mm, "radius": 2.31 * mm});
            skCircle(sketch, "E11.4.5.0", {"center": v(-57.15, 50.8) * mm, "radius": 2.31 * mm});
            skCircle(sketch, "E11.4.6.0", {"center": v(-57.15, 38.1) * mm, "radius": 2.31 * mm});
            skCircle(sketch, "E11.4.7.0", {"center": v(-57.15, 25.4) * mm, "radius": 2.31 * mm});
            skCircle(sketch, "E11.4.8.0", {"center": v(-57.15, 12.7) * mm, "radius": 2.31 * mm});
            skCircle(sketch, "E11.4.9.0", {"center": v(-57.15, 0) * mm, "radius": 2.31 * mm});
            skCircle(sketch, "E11.4.10.0", {"center": v(-57.15, -12.7) * mm, "radius": 2.31 * mm});
            skCircle(sketch, "E11.4.11.0", {"center": v(-57.15, -25.4) * mm, "radius": 2.31 * mm});
            skCircle(sketch, "E11.4.12.0", {"center": v(-57.15, -38.1) * mm, "radius": 2.31 * mm});
            skCircle(sketch, "E11.4.13.0", {"center": v(-57.15, -50.8) * mm, "radius": 2.31 * mm});
            skCircle(sketch, "E11.4.14.0", {"center": v(-57.15, -63.5) * mm, "radius": 2.31 * mm});
            skCircle(sketch, "E11.4.15.0", {"center": v(-57.15, -76.2) * mm, "radius": 2.31 * mm});
            skCircle(sketch, "E11.4.16.0", {"center": v(-57.15, -88.9) * mm, "radius": 2.31 * mm});
            skCircle(sketch, "E11.4.17.0", {"center": v(-57.15, -101.6) * mm, "radius": 2.31 * mm});
            skCircle(sketch, "E11.4.18.0", {"center": v(-57.15, -114.3) * mm, "radius": 2.31 * mm});
            skCircle(sketch, "E11.5.0.0", {"center": v(-69.85, 114.3) * mm, "radius": 2.31 * mm});
            skCircle(sketch, "E11.5.1.0", {"center": v(-69.85, 101.6) * mm, "radius": 2.31 * mm});
            skCircle(sketch, "E11.5.2.0", {"center": v(-69.85, 88.9) * mm, "radius": 2.31 * mm});
            skCircle(sketch, "E11.5.3.0", {"center": v(-69.85, 76.2) * mm, "radius": 2.31 * mm});
            skCircle(sketch, "E11.5.4.0", {"center": v(-69.85, 63.5) * mm, "radius": 2.31 * mm});
            skCircle(sketch, "E11.5.5.0", {"center": v(-69.85, 50.8) * mm, "radius": 2.31 * mm});
            skCircle(sketch, "E11.5.6.0", {"center": v(-69.85, 38.1) * mm, "radius": 2.31 * mm});
            skCircle(sketch, "E11.5.7.0", {"center": v(-69.85, 25.4) * mm, "radius": 2.31 * mm});
            skCircle(sketch, "E11.5.8.0", {"center": v(-69.85, 12.7) * mm, "radius": 2.31 * mm});
            skCircle(sketch, "E11.5.9.0", {"center": v(-69.85, 0) * mm, "radius": 2.31 * mm});
            skCircle(sketch, "E11.5.10.0", {"center": v(-69.85, -12.7) * mm, "radius": 2.31 * mm});
            skCircle(sketch, "E11.5.11.0", {"center": v(-69.85, -25.4) * mm, "radius": 2.31 * mm});
            skCircle(sketch, "E11.5.12.0", {"center": v(-69.85, -38.1) * mm, "radius": 2.31 * mm});
            skCircle(sketch, "E11.5.13.0", {"center": v(-69.85, -50.8) * mm, "radius": 2.31 * mm});
            skCircle(sketch, "E11.5.14.0", {"center": v(-69.85, -63.5) * mm, "radius": 2.31 * mm});
            skCircle(sketch, "E11.5.15.0", {"center": v(-69.85, -76.2) * mm, "radius": 2.31 * mm});
            skCircle(sketch, "E11.5.16.0", {"center": v(-69.85, -88.9) * mm, "radius": 2.31 * mm});
            skCircle(sketch, "E11.5.17.0", {"center": v(-69.85, -101.6) * mm, "radius": 2.31 * mm});
            skCircle(sketch, "E11.5.18.0", {"center": v(-69.85, -114.3) * mm, "radius": 2.31 * mm});
            skLineSegment(sketch, "E11.direction1", {"start": v(-6.35, 114.3) * mm, "end": v(-19.05, 114.3) * mm, "construction": true});
            skLineSegment(sketch, "E11.direction2", {"start": v(-6.35, 114.3) * mm, "end": v(-6.35, 101.6) * mm, "construction": true});
            skCircle(sketch, "E12", {"center": v(-24.13, -72.39) * mm, "radius": 1.6 * mm});
            skCircle(sketch, "E13", {"center": v(24.13, -73.66) * mm, "radius": 1.6 * mm});
            skCircle(sketch, "E14", {"center": v(-19.05, -124.46) * mm, "radius": 1.6 * mm});
            skCircle(sketch, "E15", {"center": v(8.9, -124.46) * mm, "radius": 1.6 * mm});
            skSolve(sketch);
        }
        {
            var Q0;
            Q0 = qSketchRegion(id + "F0", true);
            extrude(context, id + "F1", {"entities" : qUnion([Q0]), "depth" : 3.17 * mm});
        }
        {
            var Q0;
            Q0=makeQuery(id+"F1.opExtrude","CAP_FACE",FACE,{"disambiguationData":[OSD([sQuery(id+"F0.wireOp",EDGE,"E0.rect.top"),sQuery(id+"F0.wireOp",EDGE,"E0.rect.left"),sQuery(id+"F0.wireOp",EDGE,"E0.rect.right"),sQuery(id+"F0.wireOp",EDGE,"E1"),sQuery(id+"F0.wireOp",EDGE,"E2"),sQuery(id+"F0.wireOp",EDGE,"E3.bottom"),sQuery(id+"F0.wireOp",EDGE,"E4"),sQuery(id+"F0.wireOp",EDGE,"E5.0.1.0"),sQuery(id+"F0.wireOp",EDGE,"E5.0.2.0"),sQuery(id+"F0.wireOp",EDGE,"E5.0.3.0"),sQuery(id+"F0.wireOp",EDGE,"E5.0.4.0"),sQuery(id+"F0.wireOp",EDGE,"E5.0.5.0"),sQuery(id+"F0.wireOp",EDGE,"E5.0.6.0"),sQuery(id+"F0.wireOp",EDGE,"E5.0.7.0"),sQuery(id+"F0.wireOp",EDGE,"E5.0.8.0"),sQuery(id+"F0.wireOp",EDGE,"E5.0.9.0"),sQuery(id+"F0.wireOp",EDGE,"E5.0.10.0"),sQuery(id+"F0.wireOp",EDGE,"E5.0.11.0"),sQuery(id+"F0.wireOp",EDGE,"E5.0.12.0"),sQuery(id+"F0.wireOp",EDGE,"E5.0.13.0"),sQuery(id+"F0.wireOp",EDGE,"E5.1.0.0"),sQuery(id+"F0.wireOp",EDGE,"E5.1.1.0"),sQuery(id+"F0.wireOp",EDGE,"E5.1.2.0"),sQuery(id+"F0.wireOp",EDGE,"E5.1.3.0"),sQuery(id+"F0.wireOp",EDGE,"E5.1.4.0"),sQuery(id+"F0.wireOp",EDGE,"E5.1.5.0"),sQuery(id+"F0.wireOp",EDGE,"E5.1.6.0"),sQuery(id+"F0.wireOp",EDGE,"E5.1.7.0"),sQuery(id+"F0.wireOp",EDGE,"E5.1.8.0"),sQuery(id+"F0.wireOp",EDGE,"E5.1.9.0"),sQuery(id+"F0.wireOp",EDGE,"E5.1.10.0"),sQuery(id+"F0.wireOp",EDGE,"E5.1.11.0"),sQuery(id+"F0.wireOp",EDGE,"E5.1.12.0"),sQuery(id+"F0.wireOp",EDGE,"E5.1.13.0"),sQuery(id+"F0.wireOp",EDGE,"E5.2.0.0"),sQuery(id+"F0.wireOp",EDGE,"E5.2.1.0"),sQuery(id+"F0.wireOp",EDGE,"E5.2.2.0"),sQuery(id+"F0.wireOp",EDGE,"E5.2.3.0"),sQuery(id+"F0.wireOp",EDGE,"E5.2.4.0"),sQuery(id+"F0.wireOp",EDGE,"E5.2.5.0"),sQuery(id+"F0.wireOp",EDGE,"E5.2.6.0"),sQuery(id+"F0.wireOp",EDGE,"E5.2.7.0"),sQuery(id+"F0.wireOp",EDGE,"E5.2.8.0"),sQuery(id+"F0.wireOp",EDGE,"E5.2.9.0"),sQuery(id+"F0.wireOp",EDGE,"E5.2.10.0"),sQuery(id+"F0.wireOp",EDGE,"E5.2.11.0"),sQuery(id+"F0.wireOp",EDGE,"E5.2.12.0"),sQuery(id+"F0.wireOp",EDGE,"E5.2.13.0"),sQuery(id+"F0.wireOp",EDGE,"E5.3.0.0"),sQuery(id+"F0.wireOp",EDGE,"E5.3.1.0"),sQuery(id+"F0.wireOp",EDGE,"E5.3.2.0"),sQuery(id+"F0.wireOp",EDGE,"E5.3.3.0"),sQuery(id+"F0.wireOp",EDGE,"E5.3.4.0"),sQuery(id+"F0.wireOp",EDGE,"E5.3.5.0"),sQuery(id+"F0.wireOp",EDGE,"E5.3.6.0"),sQuery(id+"F0.wireOp",EDGE,"E5.3.7.0"),sQuery(id+"F0.wireOp",EDGE,"E5.3.8.0"),sQuery(id+"F0.wireOp",EDGE,"E5.3.9.0"),sQuery(id+"F0.wireOp",EDGE,"E5.3.10.0"),sQuery(id+"F0.wireOp",EDGE,"E5.3.11.0"),sQuery(id+"F0.wireOp",EDGE,"E5.3.12.0"),sQuery(id+"F0.wireOp",EDGE,"E5.3.13.0"),sQuery(id+"F0.wireOp",EDGE,"E5.3.14.0"),sQuery(id+"F0.wireOp",EDGE,"E5.3.15.0"),sQuery(id+"F0.wireOp",EDGE,"E5.3.16.0"),sQuery(id+"F0.wireOp",EDGE,"E5.3.17.0"),sQuery(id+"F0.wireOp",EDGE,"E5.3.18.0"),sQuery(id+"F0.wireOp",EDGE,"E5.3.19.0"),sQuery(id+"F0.wireOp",EDGE,"E5.4.0.0"),sQuery(id+"F0.wireOp",EDGE,"E5.4.1.0"),sQuery(id+"F0.wireOp",EDGE,"E5.4.2.0"),sQuery(id+"F0.wireOp",EDGE,"E5.4.3.0"),sQuery(id+"F0.wireOp",EDGE,"E5.4.4.0"),sQuery(id+"F0.wireOp",EDGE,"E5.4.5.0"),sQuery(id+"F0.wireOp",EDGE,"E5.4.6.0"),sQuery(id+"F0.wireOp",EDGE,"E5.4.7.0"),sQuery(id+"F0.wireOp",EDGE,"E5.4.8.0"),sQuery(id+"F0.wireOp",EDGE,"E5.4.9.0"),sQuery(id+"F0.wireOp",EDGE,"E5.4.10.0"),sQuery(id+"F0.wireOp",EDGE,"E5.4.11.0"),sQuery(id+"F0.wireOp",EDGE,"E5.4.12.0"),sQuery(id+"F0.wireOp",EDGE,"E5.4.13.0"),sQuery(id+"F0.wireOp",EDGE,"E5.4.14.0"),sQuery(id+"F0.wireOp",EDGE,"E5.4.15.0"),sQuery(id+"F0.wireOp",EDGE,"E5.4.16.0"),sQuery(id+"F0.wireOp",EDGE,"E5.4.17.0"),sQuery(id+"F0.wireOp",EDGE,"E5.4.18.0"),sQuery(id+"F0.wireOp",EDGE,"E5.4.19.0"),sQuery(id+"F0.wireOp",EDGE,"E5.5.0.0"),sQuery(id+"F0.wireOp",EDGE,"E5.5.1.0"),sQuery(id+"F0.wireOp",EDGE,"E5.5.2.0"),sQuery(id+"F0.wireOp",EDGE,"E5.5.3.0"),sQuery(id+"F0.wireOp",EDGE,"E5.5.4.0"),sQuery(id+"F0.wireOp",EDGE,"E5.5.5.0"),sQuery(id+"F0.wireOp",EDGE,"E5.5.6.0"),sQuery(id+"F0.wireOp",EDGE,"E5.5.7.0"),sQuery(id+"F0.wireOp",EDGE,"E5.5.8.0"),sQuery(id+"F0.wireOp",EDGE,"E5.5.9.0"),sQuery(id+"F0.wireOp",EDGE,"E5.5.10.0"),sQuery(id+"F0.wireOp",EDGE,"E5.5.11.0"),sQuery(id+"F0.wireOp",EDGE,"E5.5.12.0"),sQuery(id+"F0.wireOp",EDGE,"E5.5.13.0"),sQuery(id+"F0.wireOp",EDGE,"E5.5.14.0"),sQuery(id+"F0.wireOp",EDGE,"E5.5.15.0"),sQuery(id+"F0.wireOp",EDGE,"E5.5.16.0"),sQuery(id+"F0.wireOp",EDGE,"E5.5.17.0"),sQuery(id+"F0.wireOp",EDGE,"E5.5.18.0"),sQuery(id+"F0.wireOp",EDGE,"E5.5.19.0"),sQuery(id+"F0.wireOp",EDGE,"E6"),sQuery(id+"F0.wireOp",EDGE,"E7.0.1.0"),sQuery(id+"F0.wireOp",EDGE,"E7.0.2.0"),sQuery(id+"F0.wireOp",EDGE,"E7.0.3.0"),sQuery(id+"F0.wireOp",EDGE,"E7.0.4.0"),sQuery(id+"F0.wireOp",EDGE,"E7.0.5.0"),sQuery(id+"F0.wireOp",EDGE,"E7.0.6.0"),sQuery(id+"F0.wireOp",EDGE,"E7.0.7.0"),sQuery(id+"F0.wireOp",EDGE,"E7.0.8.0"),sQuery(id+"F0.wireOp",EDGE,"E7.0.9.0"),sQuery(id+"F0.wireOp",EDGE,"E7.0.10.0"),sQuery(id+"F0.wireOp",EDGE,"E7.0.11.0"),sQuery(id+"F0.wireOp",EDGE,"E7.0.12.0"),sQuery(id+"F0.wireOp",EDGE,"E7.0.13.0"),sQuery(id+"F0.wireOp",EDGE,"E7.1.0.0"),sQuery(id+"F0.wireOp",EDGE,"E7.1.1.0"),sQuery(id+"F0.wireOp",EDGE,"E7.1.2.0"),sQuery(id+"F0.wireOp",EDGE,"E7.1.3.0"),sQuery(id+"F0.wireOp",EDGE,"E7.1.4.0"),sQuery(id+"F0.wireOp",EDGE,"E7.1.5.0"),sQuery(id+"F0.wireOp",EDGE,"E7.1.6.0"),sQuery(id+"F0.wireOp",EDGE,"E7.1.7.0"),sQuery(id+"F0.wireOp",EDGE,"E7.1.8.0"),sQuery(id+"F0.wireOp",EDGE,"E7.1.9.0"),sQuery(id+"F0.wireOp",EDGE,"E7.1.10.0"),sQuery(id+"F0.wireOp",EDGE,"E7.1.11.0"),sQuery(id+"F0.wireOp",EDGE,"E7.1.12.0"),sQuery(id+"F0.wireOp",EDGE,"E7.1.13.0"),sQuery(id+"F0.wireOp",EDGE,"E7.2.0.0"),sQuery(id+"F0.wireOp",EDGE,"E7.2.1.0"),sQuery(id+"F0.wireOp",EDGE,"E7.2.2.0"),sQuery(id+"F0.wireOp",EDGE,"E7.2.3.0"),sQuery(id+"F0.wireOp",EDGE,"E7.2.4.0"),sQuery(id+"F0.wireOp",EDGE,"E7.2.5.0"),sQuery(id+"F0.wireOp",EDGE,"E7.2.6.0"),sQuery(id+"F0.wireOp",EDGE,"E7.2.7.0"),sQuery(id+"F0.wireOp",EDGE,"E7.2.8.0"),sQuery(id+"F0.wireOp",EDGE,"E7.2.9.0"),sQuery(id+"F0.wireOp",EDGE,"E7.2.10.0"),sQuery(id+"F0.wireOp",EDGE,"E7.2.11.0"),sQuery(id+"F0.wireOp",EDGE,"E7.2.12.0"),sQuery(id+"F0.wireOp",EDGE,"E7.2.13.0"),sQuery(id+"F0.wireOp",EDGE,"E7.2.14.0"),sQuery(id+"F0.wireOp",EDGE,"E7.2.15.0"),sQuery(id+"F0.wireOp",EDGE,"E7.2.16.0"),sQuery(id+"F0.wireOp",EDGE,"E7.2.17.0"),sQuery(id+"F0.wireOp",EDGE,"E7.2.18.0"),sQuery(id+"F0.wireOp",EDGE,"E7.2.19.0"),sQuery(id+"F0.wireOp",EDGE,"E7.3.0.0"),sQuery(id+"F0.wireOp",EDGE,"E7.3.1.0"),sQuery(id+"F0.wireOp",EDGE,"E7.3.2.0"),sQuery(id+"F0.wireOp",EDGE,"E7.3.3.0"),sQuery(id+"F0.wireOp",EDGE,"E7.3.4.0"),sQuery(id+"F0.wireOp",EDGE,"E7.3.5.0"),sQuery(id+"F0.wireOp",EDGE,"E7.3.6.0"),sQuery(id+"F0.wireOp",EDGE,"E7.3.7.0"),sQuery(id+"F0.wireOp",EDGE,"E7.3.8.0"),sQuery(id+"F0.wireOp",EDGE,"E7.3.9.0"),sQuery(id+"F0.wireOp",EDGE,"E7.3.10.0"),sQuery(id+"F0.wireOp",EDGE,"E7.3.11.0"),sQuery(id+"F0.wireOp",EDGE,"E7.3.12.0"),sQuery(id+"F0.wireOp",EDGE,"E7.3.13.0"),sQuery(id+"F0.wireOp",EDGE,"E7.3.14.0"),sQuery(id+"F0.wireOp",EDGE,"E7.3.15.0"),sQuery(id+"F0.wireOp",EDGE,"E7.3.16.0"),sQuery(id+"F0.wireOp",EDGE,"E7.3.17.0"),sQuery(id+"F0.wireOp",EDGE,"E7.3.18.0"),sQuery(id+"F0.wireOp",EDGE,"E7.3.19.0"),sQuery(id+"F0.wireOp",EDGE,"E7.4.0.0"),sQuery(id+"F0.wireOp",EDGE,"E7.4.1.0"),sQuery(id+"F0.wireOp",EDGE,"E7.4.2.0"),sQuery(id+"F0.wireOp",EDGE,"E7.4.3.0"),sQuery(id+"F0.wireOp",EDGE,"E7.4.4.0"),sQuery(id+"F0.wireOp",EDGE,"E7.4.5.0"),sQuery(id+"F0.wireOp",EDGE,"E7.4.6.0"),sQuery(id+"F0.wireOp",EDGE,"E7.4.7.0"),sQuery(id+"F0.wireOp",EDGE,"E7.4.8.0"),sQuery(id+"F0.wireOp",EDGE,"E7.4.9.0"),sQuery(id+"F0.wireOp",EDGE,"E7.4.10.0"),sQuery(id+"F0.wireOp",EDGE,"E7.4.11.0"),sQuery(id+"F0.wireOp",EDGE,"E7.4.12.0"),sQuery(id+"F0.wireOp",EDGE,"E7.4.13.0"),sQuery(id+"F0.wireOp",EDGE,"E7.4.14.0"),sQuery(id+"F0.wireOp",EDGE,"E7.4.15.0"),sQuery(id+"F0.wireOp",EDGE,"E7.4.16.0"),sQuery(id+"F0.wireOp",EDGE,"E7.4.17.0"),sQuery(id+"F0.wireOp",EDGE,"E7.4.18.0"),sQuery(id+"F0.wireOp",EDGE,"E7.4.19.0"),sQuery(id+"F0.wireOp",EDGE,"E8"),sQuery(id+"F0.wireOp",EDGE,"E9.0.1.0"),sQuery(id+"F0.wireOp",EDGE,"E9.0.2.0"),sQuery(id+"F0.wireOp",EDGE,"E9.0.3.0"),sQuery(id+"F0.wireOp",EDGE,"E9.0.4.0"),sQuery(id+"F0.wireOp",EDGE,"E9.0.5.0"),sQuery(id+"F0.wireOp",EDGE,"E9.0.6.0"),sQuery(id+"F0.wireOp",EDGE,"E9.0.7.0"),sQuery(id+"F0.wireOp",EDGE,"E9.0.8.0"),sQuery(id+"F0.wireOp",EDGE,"E9.0.9.0"),sQuery(id+"F0.wireOp",EDGE,"E9.0.10.0"),sQuery(id+"F0.wireOp",EDGE,"E9.0.11.0"),sQuery(id+"F0.wireOp",EDGE,"E9.0.12.0"),sQuery(id+"F0.wireOp",EDGE,"E9.0.13.0"),sQuery(id+"F0.wireOp",EDGE,"E9.1.0.0"),sQuery(id+"F0.wireOp",EDGE,"E9.1.1.0"),sQuery(id+"F0.wireOp",EDGE,"E9.1.2.0"),sQuery(id+"F0.wireOp",EDGE,"E9.1.3.0"),sQuery(id+"F0.wireOp",EDGE,"E9.1.4.0"),sQuery(id+"F0.wireOp",EDGE,"E9.1.5.0"),sQuery(id+"F0.wireOp",EDGE,"E9.1.6.0"),sQuery(id+"F0.wireOp",EDGE,"E9.1.7.0"),sQuery(id+"F0.wireOp",EDGE,"E9.1.8.0"),sQuery(id+"F0.wireOp",EDGE,"E9.1.9.0"),sQuery(id+"F0.wireOp",EDGE,"E9.1.10.0"),sQuery(id+"F0.wireOp",EDGE,"E9.1.11.0"),sQuery(id+"F0.wireOp",EDGE,"E9.1.12.0"),sQuery(id+"F0.wireOp",EDGE,"E9.1.13.0"),sQuery(id+"F0.wireOp",EDGE,"E9.2.0.0"),sQuery(id+"F0.wireOp",EDGE,"E9.2.1.0"),sQuery(id+"F0.wireOp",EDGE,"E9.2.2.0"),sQuery(id+"F0.wireOp",EDGE,"E9.2.3.0"),sQuery(id+"F0.wireOp",EDGE,"E9.2.4.0"),sQuery(id+"F0.wireOp",EDGE,"E9.2.5.0"),sQuery(id+"F0.wireOp",EDGE,"E9.2.6.0"),sQuery(id+"F0.wireOp",EDGE,"E9.2.7.0"),sQuery(id+"F0.wireOp",EDGE,"E9.2.8.0"),sQuery(id+"F0.wireOp",EDGE,"E9.2.9.0"),sQuery(id+"F0.wireOp",EDGE,"E9.2.10.0"),sQuery(id+"F0.wireOp",EDGE,"E9.2.11.0"),sQuery(id+"F0.wireOp",EDGE,"E9.2.12.0"),sQuery(id+"F0.wireOp",EDGE,"E9.2.13.0"),sQuery(id+"F0.wireOp",EDGE,"E9.2.14.0"),sQuery(id+"F0.wireOp",EDGE,"E9.2.15.0"),sQuery(id+"F0.wireOp",EDGE,"E9.2.16.0"),sQuery(id+"F0.wireOp",EDGE,"E9.2.17.0"),sQuery(id+"F0.wireOp",EDGE,"E9.2.18.0"),sQuery(id+"F0.wireOp",EDGE,"E9.3.0.0"),sQuery(id+"F0.wireOp",EDGE,"E9.3.1.0"),sQuery(id+"F0.wireOp",EDGE,"E9.3.2.0"),sQuery(id+"F0.wireOp",EDGE,"E9.3.3.0"),sQuery(id+"F0.wireOp",EDGE,"E9.3.4.0"),sQuery(id+"F0.wireOp",EDGE,"E9.3.5.0"),sQuery(id+"F0.wireOp",EDGE,"E9.3.6.0"),sQuery(id+"F0.wireOp",EDGE,"E9.3.7.0"),sQuery(id+"F0.wireOp",EDGE,"E9.3.8.0"),sQuery(id+"F0.wireOp",EDGE,"E9.3.9.0"),sQuery(id+"F0.wireOp",EDGE,"E9.3.10.0"),sQuery(id+"F0.wireOp",EDGE,"E9.3.11.0"),sQuery(id+"F0.wireOp",EDGE,"E9.3.12.0"),sQuery(id+"F0.wireOp",EDGE,"E9.3.13.0"),sQuery(id+"F0.wireOp",EDGE,"E9.3.14.0"),sQuery(id+"F0.wireOp",EDGE,"E9.3.15.0"),sQuery(id+"F0.wireOp",EDGE,"E9.3.16.0"),sQuery(id+"F0.wireOp",EDGE,"E9.3.17.0"),sQuery(id+"F0.wireOp",EDGE,"E9.3.18.0"),sQuery(id+"F0.wireOp",EDGE,"E9.4.0.0"),sQuery(id+"F0.wireOp",EDGE,"E9.4.1.0"),sQuery(id+"F0.wireOp",EDGE,"E9.4.2.0"),sQuery(id+"F0.wireOp",EDGE,"E9.4.3.0"),sQuery(id+"F0.wireOp",EDGE,"E9.4.4.0"),sQuery(id+"F0.wireOp",EDGE,"E9.4.5.0"),sQuery(id+"F0.wireOp",EDGE,"E9.4.6.0"),sQuery(id+"F0.wireOp",EDGE,"E9.4.7.0"),sQuery(id+"F0.wireOp",EDGE,"E9.4.8.0"),sQuery(id+"F0.wireOp",EDGE,"E9.4.9.0"),sQuery(id+"F0.wireOp",EDGE,"E9.4.10.0"),sQuery(id+"F0.wireOp",EDGE,"E9.4.11.0"),sQuery(id+"F0.wireOp",EDGE,"E9.4.12.0"),sQuery(id+"F0.wireOp",EDGE,"E9.4.13.0"),sQuery(id+"F0.wireOp",EDGE,"E9.4.14.0"),sQuery(id+"F0.wireOp",EDGE,"E9.4.15.0"),sQuery(id+"F0.wireOp",EDGE,"E9.4.16.0"),sQuery(id+"F0.wireOp",EDGE,"E9.4.17.0"),sQuery(id+"F0.wireOp",EDGE,"E9.4.18.0"),sQuery(id+"F0.wireOp",EDGE,"E9.5.0.0"),sQuery(id+"F0.wireOp",EDGE,"E9.5.1.0"),sQuery(id+"F0.wireOp",EDGE,"E9.5.2.0"),sQuery(id+"F0.wireOp",EDGE,"E9.5.3.0"),sQuery(id+"F0.wireOp",EDGE,"E9.5.4.0"),sQuery(id+"F0.wireOp",EDGE,"E9.5.5.0"),sQuery(id+"F0.wireOp",EDGE,"E9.5.6.0"),sQuery(id+"F0.wireOp",EDGE,"E9.5.7.0"),sQuery(id+"F0.wireOp",EDGE,"E9.5.8.0"),sQuery(id+"F0.wireOp",EDGE,"E9.5.9.0"),sQuery(id+"F0.wireOp",EDGE,"E9.5.10.0"),sQuery(id+"F0.wireOp",EDGE,"E9.5.11.0"),sQuery(id+"F0.wireOp",EDGE,"E9.5.12.0"),sQuery(id+"F0.wireOp",EDGE,"E9.5.13.0"),sQuery(id+"F0.wireOp",EDGE,"E9.5.14.0"),sQuery(id+"F0.wireOp",EDGE,"E9.5.15.0"),sQuery(id+"F0.wireOp",EDGE,"E9.5.16.0"),sQuery(id+"F0.wireOp",EDGE,"E9.5.17.0"),sQuery(id+"F0.wireOp",EDGE,"E9.5.18.0"),sQuery(id+"F0.wireOp",EDGE,"E10"),sQuery(id+"F0.wireOp",EDGE,"E11.0.1.0"),sQuery(id+"F0.wireOp",EDGE,"E11.0.2.0"),sQuery(id+"F0.wireOp",EDGE,"E11.0.3.0"),sQuery(id+"F0.wireOp",EDGE,"E11.0.4.0"),sQuery(id+"F0.wireOp",EDGE,"E11.0.5.0"),sQuery(id+"F0.wireOp",EDGE,"E11.0.6.0"),sQuery(id+"F0.wireOp",EDGE,"E11.0.7.0"),sQuery(id+"F0.wireOp",EDGE,"E11.0.8.0"),sQuery(id+"F0.wireOp",EDGE,"E11.0.9.0"),sQuery(id+"F0.wireOp",EDGE,"E11.0.10.0"),sQuery(id+"F0.wireOp",EDGE,"E11.0.11.0"),sQuery(id+"F0.wireOp",EDGE,"E11.0.12.0"),sQuery(id+"F0.wireOp",EDGE,"E11.0.13.0"),sQuery(id+"F0.wireOp",EDGE,"E11.1.0.0"),sQuery(id+"F0.wireOp",EDGE,"E11.1.1.0"),sQuery(id+"F0.wireOp",EDGE,"E11.1.2.0"),sQuery(id+"F0.wireOp",EDGE,"E11.1.3.0"),sQuery(id+"F0.wireOp",EDGE,"E11.1.4.0"),sQuery(id+"F0.wireOp",EDGE,"E11.1.5.0"),sQuery(id+"F0.wireOp",EDGE,"E11.1.6.0"),sQuery(id+"F0.wireOp",EDGE,"E11.1.7.0"),sQuery(id+"F0.wireOp",EDGE,"E11.1.8.0"),sQuery(id+"F0.wireOp",EDGE,"E11.1.9.0"),sQuery(id+"F0.wireOp",EDGE,"E11.1.10.0"),sQuery(id+"F0.wireOp",EDGE,"E11.1.11.0"),sQuery(id+"F0.wireOp",EDGE,"E11.1.12.0"),sQuery(id+"F0.wireOp",EDGE,"E11.1.13.0"),sQuery(id+"F0.wireOp",EDGE,"E11.2.0.0"),sQuery(id+"F0.wireOp",EDGE,"E11.2.1.0"),sQuery(id+"F0.wireOp",EDGE,"E11.2.2.0"),sQuery(id+"F0.wireOp",EDGE,"E11.2.3.0"),sQuery(id+"F0.wireOp",EDGE,"E11.2.4.0"),sQuery(id+"F0.wireOp",EDGE,"E11.2.5.0"),sQuery(id+"F0.wireOp",EDGE,"E11.2.6.0"),sQuery(id+"F0.wireOp",EDGE,"E11.2.7.0"),sQuery(id+"F0.wireOp",EDGE,"E11.2.8.0"),sQuery(id+"F0.wireOp",EDGE,"E11.2.9.0"),sQuery(id+"F0.wireOp",EDGE,"E11.2.10.0"),sQuery(id+"F0.wireOp",EDGE,"E11.2.11.0"),sQuery(id+"F0.wireOp",EDGE,"E11.2.12.0"),sQuery(id+"F0.wireOp",EDGE,"E11.2.13.0"),sQuery(id+"F0.wireOp",EDGE,"E11.2.14.0"),sQuery(id+"F0.wireOp",EDGE,"E11.2.15.0"),sQuery(id+"F0.wireOp",EDGE,"E11.2.16.0"),sQuery(id+"F0.wireOp",EDGE,"E11.2.17.0"),sQuery(id+"F0.wireOp",EDGE,"E11.2.18.0"),sQuery(id+"F0.wireOp",EDGE,"E11.3.0.0"),sQuery(id+"F0.wireOp",EDGE,"E11.3.1.0"),sQuery(id+"F0.wireOp",EDGE,"E11.3.2.0"),sQuery(id+"F0.wireOp",EDGE,"E11.3.3.0"),sQuery(id+"F0.wireOp",EDGE,"E11.3.4.0"),sQuery(id+"F0.wireOp",EDGE,"E11.3.5.0"),sQuery(id+"F0.wireOp",EDGE,"E11.3.6.0"),sQuery(id+"F0.wireOp",EDGE,"E11.3.7.0"),sQuery(id+"F0.wireOp",EDGE,"E11.3.8.0"),sQuery(id+"F0.wireOp",EDGE,"E11.3.9.0"),sQuery(id+"F0.wireOp",EDGE,"E11.3.10.0"),sQuery(id+"F0.wireOp",EDGE,"E11.3.11.0"),sQuery(id+"F0.wireOp",EDGE,"E11.3.12.0"),sQuery(id+"F0.wireOp",EDGE,"E11.3.13.0"),sQuery(id+"F0.wireOp",EDGE,"E11.3.14.0"),sQuery(id+"F0.wireOp",EDGE,"E11.3.15.0"),sQuery(id+"F0.wireOp",EDGE,"E11.3.16.0"),sQuery(id+"F0.wireOp",EDGE,"E11.3.17.0"),sQuery(id+"F0.wireOp",EDGE,"E11.3.18.0"),sQuery(id+"F0.wireOp",EDGE,"E11.4.0.0"),sQuery(id+"F0.wireOp",EDGE,"E11.4.1.0"),sQuery(id+"F0.wireOp",EDGE,"E11.4.2.0"),sQuery(id+"F0.wireOp",EDGE,"E11.4.3.0"),sQuery(id+"F0.wireOp",EDGE,"E11.4.4.0"),sQuery(id+"F0.wireOp",EDGE,"E11.4.5.0"),sQuery(id+"F0.wireOp",EDGE,"E11.4.6.0"),sQuery(id+"F0.wireOp",EDGE,"E11.4.7.0"),sQuery(id+"F0.wireOp",EDGE,"E11.4.8.0"),sQuery(id+"F0.wireOp",EDGE,"E11.4.9.0"),sQuery(id+"F0.wireOp",EDGE,"E11.4.10.0"),sQuery(id+"F0.wireOp",EDGE,"E11.4.11.0"),sQuery(id+"F0.wireOp",EDGE,"E11.4.12.0"),sQuery(id+"F0.wireOp",EDGE,"E11.4.13.0"),sQuery(id+"F0.wireOp",EDGE,"E11.4.14.0"),sQuery(id+"F0.wireOp",EDGE,"E11.4.15.0"),sQuery(id+"F0.wireOp",EDGE,"E11.4.16.0"),sQuery(id+"F0.wireOp",EDGE,"E11.4.17.0"),sQuery(id+"F0.wireOp",EDGE,"E11.4.18.0"),sQuery(id+"F0.wireOp",EDGE,"E11.5.0.0"),sQuery(id+"F0.wireOp",EDGE,"E11.5.1.0"),sQuery(id+"F0.wireOp",EDGE,"E11.5.2.0"),sQuery(id+"F0.wireOp",EDGE,"E11.5.3.0"),sQuery(id+"F0.wireOp",EDGE,"E11.5.4.0"),sQuery(id+"F0.wireOp",EDGE,"E11.5.5.0"),sQuery(id+"F0.wireOp",EDGE,"E11.5.6.0"),sQuery(id+"F0.wireOp",EDGE,"E11.5.7.0"),sQuery(id+"F0.wireOp",EDGE,"E11.5.8.0"),sQuery(id+"F0.wireOp",EDGE,"E11.5.9.0"),sQuery(id+"F0.wireOp",EDGE,"E11.5.10.0"),sQuery(id+"F0.wireOp",EDGE,"E11.5.11.0"),sQuery(id+"F0.wireOp",EDGE,"E11.5.12.0"),sQuery(id+"F0.wireOp",EDGE,"E11.5.13.0"),sQuery(id+"F0.wireOp",EDGE,"E11.5.14.0"),sQuery(id+"F0.wireOp",EDGE,"E11.5.15.0"),sQuery(id+"F0.wireOp",EDGE,"E11.5.16.0"),sQuery(id+"F0.wireOp",EDGE,"E11.5.17.0"),sQuery(id+"F0.wireOp",EDGE,"E11.5.18.0"),sQuery(id+"F0.wireOp",EDGE,"E12"),sQuery(id+"F0.wireOp",EDGE,"E13"),sQuery(id+"F0.wireOp",EDGE,"E14"),sQuery(id+"F0.wireOp",EDGE,"E15")])],"isStart":false});
            var sketch = newSketch(context, id + "F2", { "sketchPlane" : qUnion([Q0])});
            skLineSegment(sketch, "E16.rect.bottom", {"start": v(-76.2, -127) * mm, "end": v(-73.03, -127) * mm});
            skLineSegment(sketch, "E16.rect.top", {"start": v(-76.2, 127) * mm, "end": v(-73.03, 127) * mm});
            skLineSegment(sketch, "E16.rect.left", {"start": v(-76.2, -127) * mm, "end": v(-76.2, 127) * mm});
            skLineSegment(sketch, "E16.rect.right", {"start": v(-73.03, -127) * mm, "end": v(-73.03, 127) * mm});
            skPoint(sketch, "E16.rect.middle", {"position": v(-74.61, 0) * mm});
            skSolve(sketch);
        }
        {
            var Q0;
            Q0 = qSketchRegion(id + "F2", true);
            extrude(context, id + "F3", {"entities" : qUnion([Q0]), "depth" : 31.75 * mm});
        }
        {
            var Q0;
            Q0=makeQuery(id+"F3.opExtrude","SWEPT_FACE",FACE,{"disambiguationData":[OSD([sQuery(id+"F2.wireOp",EDGE,"E16.rect.right")])]});
            var sketch = newSketch(context, id + "F4", { "sketchPlane" : qUnion([Q0])});
            skCircle(sketch, "E17", {"center": v(-19.05, 0) * mm, "radius": 2.31 * mm});
            skPoint(sketch, "E18", {"position": v(-19.05, -127) * mm});
            skCircle(sketch, "E19.0.1.0", {"center": v(-19.05, 12.7) * mm, "radius": 2.31 * mm});
            skCircle(sketch, "E19.0.2.0", {"center": v(-19.05, 25.4) * mm, "radius": 2.31 * mm});
            skCircle(sketch, "E19.0.3.0", {"center": v(-19.05, 38.1) * mm, "radius": 2.31 * mm});
            skCircle(sketch, "E19.0.4.0", {"center": v(-19.05, 50.8) * mm, "radius": 2.31 * mm});
            skCircle(sketch, "E19.0.5.0", {"center": v(-19.05, 63.5) * mm, "radius": 2.31 * mm});
            skCircle(sketch, "E19.0.6.0", {"center": v(-19.05, 76.2) * mm, "radius": 2.31 * mm});
            skCircle(sketch, "E19.0.7.0", {"center": v(-19.05, 88.9) * mm, "radius": 2.31 * mm});
            skCircle(sketch, "E19.0.8.0", {"center": v(-19.05, 101.6) * mm, "radius": 2.31 * mm});
            skCircle(sketch, "E19.0.9.0", {"center": v(-19.05, 114.3) * mm, "radius": 2.31 * mm});
            skCircle(sketch, "E19.1.0.0", {"center": v(-6.35, 0) * mm, "radius": 2.31 * mm});
            skCircle(sketch, "E19.1.1.0", {"center": v(-6.35, 12.7) * mm, "radius": 2.31 * mm});
            skCircle(sketch, "E19.1.2.0", {"center": v(-6.35, 25.4) * mm, "radius": 2.31 * mm});
            skCircle(sketch, "E19.1.3.0", {"center": v(-6.35, 38.1) * mm, "radius": 2.31 * mm});
            skCircle(sketch, "E19.1.4.0", {"center": v(-6.35, 50.8) * mm, "radius": 2.31 * mm});
            skCircle(sketch, "E19.1.5.0", {"center": v(-6.35, 63.5) * mm, "radius": 2.31 * mm});
            skCircle(sketch, "E19.1.6.0", {"center": v(-6.35, 76.2) * mm, "radius": 2.31 * mm});
            skCircle(sketch, "E19.1.7.0", {"center": v(-6.35, 88.9) * mm, "radius": 2.31 * mm});
            skCircle(sketch, "E19.1.8.0", {"center": v(-6.35, 101.6) * mm, "radius": 2.31 * mm});
            skCircle(sketch, "E19.1.9.0", {"center": v(-6.35, 114.3) * mm, "radius": 2.31 * mm});
            skLineSegment(sketch, "E19.direction1", {"start": v(-19.05, 0) * mm, "end": v(-6.35, 0) * mm, "construction": true});
            skLineSegment(sketch, "E19.direction2", {"start": v(-19.05, 0) * mm, "end": v(-19.05, 12.7) * mm, "construction": true});
            skCircle(sketch, "E20", {"center": v(-31.75, 0) * mm, "radius": 2.31 * mm});
            skCircle(sketch, "E21.0.1.0", {"center": v(-31.75, 12.7) * mm, "radius": 2.31 * mm});
            skCircle(sketch, "E21.0.2.0", {"center": v(-31.75, 25.4) * mm, "radius": 2.31 * mm});
            skCircle(sketch, "E21.0.3.0", {"center": v(-31.75, 38.1) * mm, "radius": 2.31 * mm});
            skCircle(sketch, "E21.0.4.0", {"center": v(-31.75, 50.8) * mm, "radius": 2.31 * mm});
            skCircle(sketch, "E21.0.5.0", {"center": v(-31.75, 63.5) * mm, "radius": 2.31 * mm});
            skCircle(sketch, "E21.0.6.0", {"center": v(-31.75, 76.2) * mm, "radius": 2.31 * mm});
            skCircle(sketch, "E21.0.7.0", {"center": v(-31.75, 88.9) * mm, "radius": 2.31 * mm});
            skCircle(sketch, "E21.0.8.0", {"center": v(-31.75, 101.6) * mm, "radius": 2.31 * mm});
            skCircle(sketch, "E21.0.9.0", {"center": v(-31.75, 114.3) * mm, "radius": 2.31 * mm});
            skLineSegment(sketch, "E21.direction1", {"start": v(-31.75, 0) * mm, "end": v(-31.82, -0.03) * mm, "construction": true});
            skLineSegment(sketch, "E21.direction2", {"start": v(-31.75, 0) * mm, "end": v(-31.75, 12.7) * mm, "construction": true});
            skCircle(sketch, "E22", {"center": v(-31.75, -12.7) * mm, "radius": 2.31 * mm});
            skCircle(sketch, "E23.0.1.0", {"center": v(-31.75, -25.4) * mm, "radius": 2.31 * mm});
            skCircle(sketch, "E23.0.2.0", {"center": v(-31.75, -38.1) * mm, "radius": 2.31 * mm});
            skCircle(sketch, "E23.0.3.0", {"center": v(-31.75, -50.8) * mm, "radius": 2.31 * mm});
            skCircle(sketch, "E23.0.4.0", {"center": v(-31.75, -63.5) * mm, "radius": 2.31 * mm});
            skCircle(sketch, "E23.0.5.0", {"center": v(-31.75, -76.2) * mm, "radius": 2.31 * mm});
            skCircle(sketch, "E23.0.6.0", {"center": v(-31.75, -88.9) * mm, "radius": 2.31 * mm});
            skCircle(sketch, "E23.0.7.0", {"center": v(-31.75, -101.6) * mm, "radius": 2.31 * mm});
            skCircle(sketch, "E23.0.8.0", {"center": v(-31.75, -114.3) * mm, "radius": 2.31 * mm});
            skCircle(sketch, "E23.1.0.0", {"center": v(-19.05, -12.7) * mm, "radius": 2.31 * mm});
            skCircle(sketch, "E23.1.1.0", {"center": v(-19.05, -25.4) * mm, "radius": 2.31 * mm});
            skCircle(sketch, "E23.1.2.0", {"center": v(-19.05, -38.1) * mm, "radius": 2.31 * mm});
            skCircle(sketch, "E23.1.3.0", {"center": v(-19.05, -50.8) * mm, "radius": 2.31 * mm});
            skCircle(sketch, "E23.1.4.0", {"center": v(-19.05, -63.5) * mm, "radius": 2.31 * mm});
            skCircle(sketch, "E23.1.5.0", {"center": v(-19.05, -76.2) * mm, "radius": 2.31 * mm});
            skCircle(sketch, "E23.1.6.0", {"center": v(-19.05, -88.9) * mm, "radius": 2.31 * mm});
            skCircle(sketch, "E23.1.7.0", {"center": v(-19.05, -101.6) * mm, "radius": 2.31 * mm});
            skCircle(sketch, "E23.1.8.0", {"center": v(-19.05, -114.3) * mm, "radius": 2.31 * mm});
            skCircle(sketch, "E23.2.0.0", {"center": v(-6.35, -12.7) * mm, "radius": 2.31 * mm});
            skCircle(sketch, "E23.2.1.0", {"center": v(-6.35, -25.4) * mm, "radius": 2.31 * mm});
            skCircle(sketch, "E23.2.2.0", {"center": v(-6.35, -38.1) * mm, "radius": 2.31 * mm});
            skCircle(sketch, "E23.2.3.0", {"center": v(-6.35, -50.8) * mm, "radius": 2.31 * mm});
            skCircle(sketch, "E23.2.4.0", {"center": v(-6.35, -63.5) * mm, "radius": 2.31 * mm});
            skCircle(sketch, "E23.2.5.0", {"center": v(-6.35, -76.2) * mm, "radius": 2.31 * mm});
            skCircle(sketch, "E23.2.6.0", {"center": v(-6.35, -88.9) * mm, "radius": 2.31 * mm});
            skCircle(sketch, "E23.2.7.0", {"center": v(-6.35, -101.6) * mm, "radius": 2.31 * mm});
            skCircle(sketch, "E23.2.8.0", {"center": v(-6.35, -114.3) * mm, "radius": 2.31 * mm});
            skLineSegment(sketch, "E23.direction1", {"start": v(-31.75, -12.7) * mm, "end": v(-19.05, -12.7) * mm, "construction": true});
            skLineSegment(sketch, "E23.direction2", {"start": v(-31.75, -12.7) * mm, "end": v(-31.75, -25.4) * mm, "construction": true});
            skCircle(sketch, "E24", {"center": v(-25.4, -120.65) * mm, "radius": 2.31 * mm});
            skCircle(sketch, "E25.0.1.0", {"center": v(-25.4, -107.95) * mm, "radius": 2.31 * mm});
            skCircle(sketch, "E25.0.2.0", {"center": v(-25.4, -95.25) * mm, "radius": 2.31 * mm});
            skCircle(sketch, "E25.0.3.0", {"center": v(-25.4, -82.55) * mm, "radius": 2.31 * mm});
            skCircle(sketch, "E25.0.4.0", {"center": v(-25.4, -69.85) * mm, "radius": 2.31 * mm});
            skCircle(sketch, "E25.0.5.0", {"center": v(-25.4, -57.15) * mm, "radius": 2.31 * mm});
            skCircle(sketch, "E25.0.6.0", {"center": v(-25.4, -44.45) * mm, "radius": 2.31 * mm});
            skCircle(sketch, "E25.0.7.0", {"center": v(-25.4, -31.75) * mm, "radius": 2.31 * mm});
            skCircle(sketch, "E25.0.8.0", {"center": v(-25.4, -19.05) * mm, "radius": 2.31 * mm});
            skCircle(sketch, "E25.0.9.0", {"center": v(-25.4, -6.35) * mm, "radius": 2.31 * mm});
            skCircle(sketch, "E25.0.10.0", {"center": v(-25.4, 6.35) * mm, "radius": 2.31 * mm});
            skCircle(sketch, "E25.0.11.0", {"center": v(-25.4, 19.05) * mm, "radius": 2.31 * mm});
            skCircle(sketch, "E25.0.12.0", {"center": v(-25.4, 31.75) * mm, "radius": 2.31 * mm});
            skCircle(sketch, "E25.0.13.0", {"center": v(-25.4, 44.45) * mm, "radius": 2.31 * mm});
            skCircle(sketch, "E25.0.14.0", {"center": v(-25.4, 57.15) * mm, "radius": 2.31 * mm});
            skCircle(sketch, "E25.0.15.0", {"center": v(-25.4, 69.85) * mm, "radius": 2.31 * mm});
            skCircle(sketch, "E25.0.16.0", {"center": v(-25.4, 82.55) * mm, "radius": 2.31 * mm});
            skCircle(sketch, "E25.0.17.0", {"center": v(-25.4, 95.25) * mm, "radius": 2.31 * mm});
            skCircle(sketch, "E25.0.18.0", {"center": v(-25.4, 107.95) * mm, "radius": 2.31 * mm});
            skCircle(sketch, "E25.0.19.0", {"center": v(-25.4, 120.65) * mm, "radius": 2.31 * mm});
            skCircle(sketch, "E25.1.0.0", {"center": v(-12.7, -120.65) * mm, "radius": 2.31 * mm});
            skCircle(sketch, "E25.1.1.0", {"center": v(-12.7, -107.95) * mm, "radius": 2.31 * mm});
            skCircle(sketch, "E25.1.2.0", {"center": v(-12.7, -95.25) * mm, "radius": 2.31 * mm});
            skCircle(sketch, "E25.1.3.0", {"center": v(-12.7, -82.55) * mm, "radius": 2.31 * mm});
            skCircle(sketch, "E25.1.4.0", {"center": v(-12.7, -69.85) * mm, "radius": 2.31 * mm});
            skCircle(sketch, "E25.1.5.0", {"center": v(-12.7, -57.15) * mm, "radius": 2.31 * mm});
            skCircle(sketch, "E25.1.6.0", {"center": v(-12.7, -44.45) * mm, "radius": 2.31 * mm});
            skCircle(sketch, "E25.1.7.0", {"center": v(-12.7, -31.75) * mm, "radius": 2.31 * mm});
            skCircle(sketch, "E25.1.8.0", {"center": v(-12.7, -19.05) * mm, "radius": 2.31 * mm});
            skCircle(sketch, "E25.1.9.0", {"center": v(-12.7, -6.35) * mm, "radius": 2.31 * mm});
            skCircle(sketch, "E25.1.10.0", {"center": v(-12.7, 6.35) * mm, "radius": 2.31 * mm});
            skCircle(sketch, "E25.1.11.0", {"center": v(-12.7, 19.05) * mm, "radius": 2.31 * mm});
            skCircle(sketch, "E25.1.12.0", {"center": v(-12.7, 31.75) * mm, "radius": 2.31 * mm});
            skCircle(sketch, "E25.1.13.0", {"center": v(-12.7, 44.45) * mm, "radius": 2.31 * mm});
            skCircle(sketch, "E25.1.14.0", {"center": v(-12.7, 57.15) * mm, "radius": 2.31 * mm});
            skCircle(sketch, "E25.1.15.0", {"center": v(-12.7, 69.85) * mm, "radius": 2.31 * mm});
            skCircle(sketch, "E25.1.16.0", {"center": v(-12.7, 82.55) * mm, "radius": 2.31 * mm});
            skCircle(sketch, "E25.1.17.0", {"center": v(-12.7, 95.25) * mm, "radius": 2.31 * mm});
            skCircle(sketch, "E25.1.18.0", {"center": v(-12.7, 107.95) * mm, "radius": 2.31 * mm});
            skCircle(sketch, "E25.1.19.0", {"center": v(-12.7, 120.65) * mm, "radius": 2.31 * mm});
            skLineSegment(sketch, "E25.direction1", {"start": v(-25.4, -120.65) * mm, "end": v(-12.7, -120.65) * mm, "construction": true});
            skLineSegment(sketch, "E25.direction2", {"start": v(-25.4, -120.65) * mm, "end": v(-25.4, -107.95) * mm, "construction": true});
            skSolve(sketch);
        }
        {
            var Q0;
            Q0 = qSketchRegion(id + "F4", true);
            extrude(context, id + "F5", {"entities" : qUnion([Q0]), "operationType" : NewBodyOperationType.REMOVE, "endBound" : BoundingType.THROUGH_ALL, "oppositeDirection" : true, "depth" : 25.4 * mm});
        }
        {
            var Q0;
            Q0=makeQuery(id+"F3.opExtrude","CAP_FACE",FACE,{"disambiguationData":[OSD([sQuery(id+"F2.wireOp",EDGE,"E16.rect.bottom"),sQuery(id+"F2.wireOp",EDGE,"E16.rect.top"),sQuery(id+"F2.wireOp",EDGE,"E16.rect.left"),sQuery(id+"F2.wireOp",EDGE,"E16.rect.right")])],"isStart":false});
            var sketch = newSketch(context, id + "F6", { "sketchPlane" : qUnion([Q0])});
            skLineSegment(sketch, "E26.bottom", {"start": v(-73.03, -127) * mm, "end": v(-111.13, -127) * mm});
            skLineSegment(sketch, "E26.top", {"start": v(-73.03, 127) * mm, "end": v(-111.13, 127) * mm});
            skLineSegment(sketch, "E26.left", {"start": v(-73.03, -127) * mm, "end": v(-73.03, 127) * mm});
            skLineSegment(sketch, "E26.right", {"start": v(-111.13, -127) * mm, "end": v(-111.13, 127) * mm});
            skCircle(sketch, "E27", {"center": v(-92.08, 0) * mm, "radius": 2.31 * mm});
            skPoint(sketch, "E28", {"position": v(-92.08, -127) * mm});
            skPoint(sketch, "E29", {"position": v(-111.13, 0) * mm});
            skCircle(sketch, "E30.0.1.0", {"center": v(-92.08, -12.7) * mm, "radius": 2.31 * mm});
            skCircle(sketch, "E30.0.2.0", {"center": v(-92.08, -25.4) * mm, "radius": 2.31 * mm});
            skCircle(sketch, "E30.0.3.0", {"center": v(-92.08, -38.1) * mm, "radius": 2.31 * mm});
            skCircle(sketch, "E30.0.4.0", {"center": v(-92.08, -50.8) * mm, "radius": 2.31 * mm});
            skCircle(sketch, "E30.0.5.0", {"center": v(-92.08, -63.5) * mm, "radius": 2.31 * mm});
            skCircle(sketch, "E30.0.6.0", {"center": v(-92.08, -76.2) * mm, "radius": 2.31 * mm});
            skCircle(sketch, "E30.0.7.0", {"center": v(-92.08, -88.9) * mm, "radius": 2.31 * mm});
            skCircle(sketch, "E30.0.8.0", {"center": v(-92.08, -101.6) * mm, "radius": 2.31 * mm});
            skCircle(sketch, "E30.0.9.0", {"center": v(-92.08, -114.3) * mm, "radius": 2.31 * mm});
            skCircle(sketch, "E30.1.0.0", {"center": v(-79.38, 0) * mm, "radius": 2.31 * mm});
            skCircle(sketch, "E30.1.1.0", {"center": v(-79.38, -12.7) * mm, "radius": 2.31 * mm});
            skCircle(sketch, "E30.1.2.0", {"center": v(-79.38, -25.4) * mm, "radius": 2.31 * mm});
            skCircle(sketch, "E30.1.3.0", {"center": v(-79.38, -38.1) * mm, "radius": 2.31 * mm});
            skCircle(sketch, "E30.1.4.0", {"center": v(-79.38, -50.8) * mm, "radius": 2.31 * mm});
            skCircle(sketch, "E30.1.5.0", {"center": v(-79.38, -63.5) * mm, "radius": 2.31 * mm});
            skCircle(sketch, "E30.1.6.0", {"center": v(-79.38, -76.2) * mm, "radius": 2.31 * mm});
            skCircle(sketch, "E30.1.7.0", {"center": v(-79.38, -88.9) * mm, "radius": 2.31 * mm});
            skCircle(sketch, "E30.1.8.0", {"center": v(-79.38, -101.6) * mm, "radius": 2.31 * mm});
            skCircle(sketch, "E30.1.9.0", {"center": v(-79.38, -114.3) * mm, "radius": 2.31 * mm});
            skLineSegment(sketch, "E30.direction1", {"start": v(-92.08, 0) * mm, "end": v(-79.38, 0) * mm, "construction": true});
            skLineSegment(sketch, "E30.direction2", {"start": v(-92.08, 0) * mm, "end": v(-92.08, -12.7) * mm, "construction": true});
            skCircle(sketch, "E31", {"center": v(-92.08, 12.7) * mm, "radius": 2.31 * mm});
            skCircle(sketch, "E32.0.1.0", {"center": v(-92.08, 25.4) * mm, "radius": 2.31 * mm});
            skCircle(sketch, "E32.0.2.0", {"center": v(-92.08, 38.1) * mm, "radius": 2.31 * mm});
            skCircle(sketch, "E32.0.3.0", {"center": v(-92.08, 50.8) * mm, "radius": 2.31 * mm});
            skCircle(sketch, "E32.0.4.0", {"center": v(-92.08, 63.5) * mm, "radius": 2.31 * mm});
            skCircle(sketch, "E32.0.5.0", {"center": v(-92.08, 76.2) * mm, "radius": 2.31 * mm});
            skCircle(sketch, "E32.0.6.0", {"center": v(-92.08, 88.9) * mm, "radius": 2.31 * mm});
            skCircle(sketch, "E32.0.7.0", {"center": v(-92.08, 101.6) * mm, "radius": 2.31 * mm});
            skCircle(sketch, "E32.0.8.0", {"center": v(-92.08, 114.3) * mm, "radius": 2.31 * mm});
            skCircle(sketch, "E32.1.0.0", {"center": v(-79.38, 12.7) * mm, "radius": 2.31 * mm});
            skCircle(sketch, "E32.1.1.0", {"center": v(-79.38, 25.4) * mm, "radius": 2.31 * mm});
            skCircle(sketch, "E32.1.2.0", {"center": v(-79.38, 38.1) * mm, "radius": 2.31 * mm});
            skCircle(sketch, "E32.1.3.0", {"center": v(-79.38, 50.8) * mm, "radius": 2.31 * mm});
            skCircle(sketch, "E32.1.4.0", {"center": v(-79.38, 63.5) * mm, "radius": 2.31 * mm});
            skCircle(sketch, "E32.1.5.0", {"center": v(-79.38, 76.2) * mm, "radius": 2.31 * mm});
            skCircle(sketch, "E32.1.6.0", {"center": v(-79.38, 88.9) * mm, "radius": 2.31 * mm});
            skCircle(sketch, "E32.1.7.0", {"center": v(-79.38, 101.6) * mm, "radius": 2.31 * mm});
            skCircle(sketch, "E32.1.8.0", {"center": v(-79.38, 114.3) * mm, "radius": 2.31 * mm});
            skLineSegment(sketch, "E32.direction1", {"start": v(-92.08, 12.7) * mm, "end": v(-79.38, 12.7) * mm, "construction": true});
            skLineSegment(sketch, "E32.direction2", {"start": v(-92.08, 12.7) * mm, "end": v(-92.08, 25.4) * mm, "construction": true});
            skCircle(sketch, "E33", {"center": v(-104.78, 114.3) * mm, "radius": 2.31 * mm});
            skCircle(sketch, "E34.0.1.0", {"center": v(-104.78, 101.6) * mm, "radius": 2.31 * mm});
            skCircle(sketch, "E34.0.2.0", {"center": v(-104.78, 88.9) * mm, "radius": 2.31 * mm});
            skCircle(sketch, "E34.0.3.0", {"center": v(-104.78, 76.2) * mm, "radius": 2.31 * mm});
            skCircle(sketch, "E34.0.4.0", {"center": v(-104.78, 63.5) * mm, "radius": 2.31 * mm});
            skCircle(sketch, "E34.0.5.0", {"center": v(-104.78, 50.8) * mm, "radius": 2.31 * mm});
            skCircle(sketch, "E34.0.6.0", {"center": v(-104.78, 38.1) * mm, "radius": 2.31 * mm});
            skCircle(sketch, "E34.0.7.0", {"center": v(-104.78, 25.4) * mm, "radius": 2.31 * mm});
            skCircle(sketch, "E34.0.8.0", {"center": v(-104.78, 12.7) * mm, "radius": 2.31 * mm});
            skCircle(sketch, "E34.0.9.0", {"center": v(-104.78, 0) * mm, "radius": 2.31 * mm});
            skCircle(sketch, "E34.0.10.0", {"center": v(-104.78, -12.7) * mm, "radius": 2.31 * mm});
            skCircle(sketch, "E34.0.11.0", {"center": v(-104.78, -25.4) * mm, "radius": 2.31 * mm});
            skCircle(sketch, "E34.0.12.0", {"center": v(-104.78, -38.1) * mm, "radius": 2.31 * mm});
            skCircle(sketch, "E34.0.13.0", {"center": v(-104.78, -50.8) * mm, "radius": 2.31 * mm});
            skCircle(sketch, "E34.0.14.0", {"center": v(-104.78, -63.5) * mm, "radius": 2.31 * mm});
            skCircle(sketch, "E34.0.15.0", {"center": v(-104.78, -76.2) * mm, "radius": 2.31 * mm});
            skCircle(sketch, "E34.0.16.0", {"center": v(-104.78, -88.9) * mm, "radius": 2.31 * mm});
            skCircle(sketch, "E34.0.17.0", {"center": v(-104.78, -101.6) * mm, "radius": 2.31 * mm});
            skCircle(sketch, "E34.0.18.0", {"center": v(-104.78, -114.3) * mm, "radius": 2.31 * mm});
            skLineSegment(sketch, "E34.direction1", {"start": v(-104.78, 114.3) * mm, "end": v(-130.18, 114.3) * mm, "construction": true});
            skLineSegment(sketch, "E34.direction2", {"start": v(-104.78, 114.3) * mm, "end": v(-104.78, 101.6) * mm, "construction": true});
            skCircle(sketch, "E35", {"center": v(-98.43, 120.65) * mm, "radius": 2.31 * mm});
            skCircle(sketch, "E36.0.1.0", {"center": v(-98.43, 107.95) * mm, "radius": 2.31 * mm});
            skCircle(sketch, "E36.0.2.0", {"center": v(-98.43, 95.25) * mm, "radius": 2.31 * mm});
            skCircle(sketch, "E36.0.3.0", {"center": v(-98.43, 82.55) * mm, "radius": 2.31 * mm});
            skCircle(sketch, "E36.0.4.0", {"center": v(-98.43, 69.85) * mm, "radius": 2.31 * mm});
            skCircle(sketch, "E36.0.5.0", {"center": v(-98.43, 57.15) * mm, "radius": 2.31 * mm});
            skCircle(sketch, "E36.0.6.0", {"center": v(-98.43, 44.45) * mm, "radius": 2.31 * mm});
            skCircle(sketch, "E36.0.7.0", {"center": v(-98.43, 31.75) * mm, "radius": 2.31 * mm});
            skCircle(sketch, "E36.0.8.0", {"center": v(-98.43, 19.05) * mm, "radius": 2.31 * mm});
            skCircle(sketch, "E36.0.9.0", {"center": v(-98.43, 6.35) * mm, "radius": 2.31 * mm});
            skCircle(sketch, "E36.0.10.0", {"center": v(-98.43, -6.35) * mm, "radius": 2.31 * mm});
            skCircle(sketch, "E36.0.11.0", {"center": v(-98.43, -19.05) * mm, "radius": 2.31 * mm});
            skCircle(sketch, "E36.0.12.0", {"center": v(-98.43, -31.75) * mm, "radius": 2.31 * mm});
            skCircle(sketch, "E36.0.13.0", {"center": v(-98.43, -44.45) * mm, "radius": 2.31 * mm});
            skCircle(sketch, "E36.0.14.0", {"center": v(-98.43, -57.15) * mm, "radius": 2.31 * mm});
            skCircle(sketch, "E36.0.15.0", {"center": v(-98.43, -69.85) * mm, "radius": 2.31 * mm});
            skCircle(sketch, "E36.0.16.0", {"center": v(-98.43, -82.55) * mm, "radius": 2.31 * mm});
            skCircle(sketch, "E36.0.17.0", {"center": v(-98.43, -95.25) * mm, "radius": 2.31 * mm});
            skCircle(sketch, "E36.0.18.0", {"center": v(-98.43, -107.95) * mm, "radius": 2.31 * mm});
            skCircle(sketch, "E36.0.19.0", {"center": v(-98.43, -120.65) * mm, "radius": 2.31 * mm});
            skCircle(sketch, "E36.1.0.0", {"center": v(-85.73, 120.65) * mm, "radius": 2.31 * mm});
            skCircle(sketch, "E36.1.1.0", {"center": v(-85.73, 107.95) * mm, "radius": 2.31 * mm});
            skCircle(sketch, "E36.1.2.0", {"center": v(-85.73, 95.25) * mm, "radius": 2.31 * mm});
            skCircle(sketch, "E36.1.3.0", {"center": v(-85.73, 82.55) * mm, "radius": 2.31 * mm});
            skCircle(sketch, "E36.1.4.0", {"center": v(-85.73, 69.85) * mm, "radius": 2.31 * mm});
            skCircle(sketch, "E36.1.5.0", {"center": v(-85.73, 57.15) * mm, "radius": 2.31 * mm});
            skCircle(sketch, "E36.1.6.0", {"center": v(-85.73, 44.45) * mm, "radius": 2.31 * mm});
            skCircle(sketch, "E36.1.7.0", {"center": v(-85.73, 31.75) * mm, "radius": 2.31 * mm});
            skCircle(sketch, "E36.1.8.0", {"center": v(-85.73, 19.05) * mm, "radius": 2.31 * mm});
            skCircle(sketch, "E36.1.9.0", {"center": v(-85.73, 6.35) * mm, "radius": 2.31 * mm});
            skCircle(sketch, "E36.1.10.0", {"center": v(-85.73, -6.35) * mm, "radius": 2.31 * mm});
            skCircle(sketch, "E36.1.11.0", {"center": v(-85.73, -19.05) * mm, "radius": 2.31 * mm});
            skCircle(sketch, "E36.1.12.0", {"center": v(-85.73, -31.75) * mm, "radius": 2.31 * mm});
            skCircle(sketch, "E36.1.13.0", {"center": v(-85.73, -44.45) * mm, "radius": 2.31 * mm});
            skCircle(sketch, "E36.1.14.0", {"center": v(-85.73, -57.15) * mm, "radius": 2.31 * mm});
            skCircle(sketch, "E36.1.15.0", {"center": v(-85.73, -69.85) * mm, "radius": 2.31 * mm});
            skCircle(sketch, "E36.1.16.0", {"center": v(-85.73, -82.55) * mm, "radius": 2.31 * mm});
            skCircle(sketch, "E36.1.17.0", {"center": v(-85.73, -95.25) * mm, "radius": 2.31 * mm});
            skCircle(sketch, "E36.1.18.0", {"center": v(-85.73, -107.95) * mm, "radius": 2.31 * mm});
            skCircle(sketch, "E36.1.19.0", {"center": v(-85.73, -120.65) * mm, "radius": 2.31 * mm});
            skLineSegment(sketch, "E36.direction1", {"start": v(-98.43, 120.65) * mm, "end": v(-85.73, 120.65) * mm, "construction": true});
            skLineSegment(sketch, "E36.direction2", {"start": v(-98.43, 120.65) * mm, "end": v(-98.43, 107.95) * mm, "construction": true});
            skSolve(sketch);
        }
        {
            var Q0;
            {var subQ1=sQuery(id+"F6.wireOp",EDGE,"E26.right");Q0=makeQuery(id+"F6.imprint","IMPRINT",FACE,{"disambiguationData":[TD([[makeQuery(id+"F6.imprint","IMPRINT",EDGE,{"derivedFrom":subQ1}),-1.0]])]});}
            var Q1;
            {var subQ1=sQuery(id+"F6.wireOp",EDGE,"E26.left");Q1=makeQuery(id+"F6.imprint","IMPRINT",FACE,{"disambiguationData":[TD([[makeQuery(id+"F6.imprint","IMPRINT",EDGE,{"derivedFrom":subQ1}),1.0]])]});}
            extrude(context, id + "F7", {"entities" : qUnion([Q0, Q1]), "depth" : 3.17 * mm});
        }
        {
            var Q0;
            Q0=makeQuery(id+"F3.opExtrude","SWEPT_BODY",BODY,{"disambiguationData":[OSD([sQuery(id+"F2.wireOp",EDGE,"E16.rect.bottom"),sQuery(id+"F2.wireOp",EDGE,"E16.rect.top"),sQuery(id+"F2.wireOp",EDGE,"E16.rect.left"),sQuery(id+"F2.wireOp",EDGE,"E16.rect.right")])]});
            var Q1;
            Q1=makeQuery(id+"F7.opExtrude","SWEPT_BODY",BODY,{"disambiguationData":[OSD([sQuery(id+"F6.wireOp",EDGE,"E26.bottom"),sQuery(id+"F6.wireOp",EDGE,"E26.top"),sQuery(id+"F6.wireOp",EDGE,"E26.left"),sQuery(id+"F6.wireOp",EDGE,"E26.right"),sQuery(id+"F6.wireOp",EDGE,"E27"),sQuery(id+"F6.wireOp",EDGE,"E30.0.1.0"),sQuery(id+"F6.wireOp",EDGE,"E30.0.2.0"),sQuery(id+"F6.wireOp",EDGE,"E30.0.3.0"),sQuery(id+"F6.wireOp",EDGE,"E30.0.4.0"),sQuery(id+"F6.wireOp",EDGE,"E30.0.5.0"),sQuery(id+"F6.wireOp",EDGE,"E30.0.6.0"),sQuery(id+"F6.wireOp",EDGE,"E30.0.7.0"),sQuery(id+"F6.wireOp",EDGE,"E30.0.8.0"),sQuery(id+"F6.wireOp",EDGE,"E30.0.9.0"),sQuery(id+"F6.wireOp",EDGE,"E30.1.0.0"),sQuery(id+"F6.wireOp",EDGE,"E30.1.1.0"),sQuery(id+"F6.wireOp",EDGE,"E30.1.2.0"),sQuery(id+"F6.wireOp",EDGE,"E30.1.3.0"),sQuery(id+"F6.wireOp",EDGE,"E30.1.4.0"),sQuery(id+"F6.wireOp",EDGE,"E30.1.5.0"),sQuery(id+"F6.wireOp",EDGE,"E30.1.6.0"),sQuery(id+"F6.wireOp",EDGE,"E30.1.7.0"),sQuery(id+"F6.wireOp",EDGE,"E30.1.8.0"),sQuery(id+"F6.wireOp",EDGE,"E30.1.9.0"),sQuery(id+"F6.wireOp",EDGE,"E31"),sQuery(id+"F6.wireOp",EDGE,"E32.0.1.0"),sQuery(id+"F6.wireOp",EDGE,"E32.0.2.0"),sQuery(id+"F6.wireOp",EDGE,"E32.0.3.0"),sQuery(id+"F6.wireOp",EDGE,"E32.0.4.0"),sQuery(id+"F6.wireOp",EDGE,"E32.0.5.0"),sQuery(id+"F6.wireOp",EDGE,"E32.0.6.0"),sQuery(id+"F6.wireOp",EDGE,"E32.0.7.0"),sQuery(id+"F6.wireOp",EDGE,"E32.0.8.0"),sQuery(id+"F6.wireOp",EDGE,"E32.1.0.0"),sQuery(id+"F6.wireOp",EDGE,"E32.1.1.0"),sQuery(id+"F6.wireOp",EDGE,"E32.1.2.0"),sQuery(id+"F6.wireOp",EDGE,"E32.1.3.0"),sQuery(id+"F6.wireOp",EDGE,"E32.1.4.0"),sQuery(id+"F6.wireOp",EDGE,"E32.1.5.0"),sQuery(id+"F6.wireOp",EDGE,"E32.1.6.0"),sQuery(id+"F6.wireOp",EDGE,"E32.1.7.0"),sQuery(id+"F6.wireOp",EDGE,"E32.1.8.0"),sQuery(id+"F6.wireOp",EDGE,"E33"),sQuery(id+"F6.wireOp",EDGE,"E34.0.1.0"),sQuery(id+"F6.wireOp",EDGE,"E34.0.2.0"),sQuery(id+"F6.wireOp",EDGE,"E34.0.3.0"),sQuery(id+"F6.wireOp",EDGE,"E34.0.4.0"),sQuery(id+"F6.wireOp",EDGE,"E34.0.5.0"),sQuery(id+"F6.wireOp",EDGE,"E34.0.6.0"),sQuery(id+"F6.wireOp",EDGE,"E34.0.7.0"),sQuery(id+"F6.wireOp",EDGE,"E34.0.8.0"),sQuery(id+"F6.wireOp",EDGE,"E34.0.9.0"),sQuery(id+"F6.wireOp",EDGE,"E34.0.10.0"),sQuery(id+"F6.wireOp",EDGE,"E34.0.11.0"),sQuery(id+"F6.wireOp",EDGE,"E34.0.12.0"),sQuery(id+"F6.wireOp",EDGE,"E34.0.13.0"),sQuery(id+"F6.wireOp",EDGE,"E34.0.14.0"),sQuery(id+"F6.wireOp",EDGE,"E34.0.15.0"),sQuery(id+"F6.wireOp",EDGE,"E34.0.16.0"),sQuery(id+"F6.wireOp",EDGE,"E34.0.17.0"),sQuery(id+"F6.wireOp",EDGE,"E34.0.18.0"),sQuery(id+"F6.wireOp",EDGE,"E35"),sQuery(id+"F6.wireOp",EDGE,"E36.0.1.0"),sQuery(id+"F6.wireOp",EDGE,"E36.0.2.0"),sQuery(id+"F6.wireOp",EDGE,"E36.0.3.0"),sQuery(id+"F6.wireOp",EDGE,"E36.0.4.0"),sQuery(id+"F6.wireOp",EDGE,"E36.0.5.0"),sQuery(id+"F6.wireOp",EDGE,"E36.0.6.0"),sQuery(id+"F6.wireOp",EDGE,"E36.0.7.0"),sQuery(id+"F6.wireOp",EDGE,"E36.0.8.0"),sQuery(id+"F6.wireOp",EDGE,"E36.0.9.0"),sQuery(id+"F6.wireOp",EDGE,"E36.0.10.0"),sQuery(id+"F6.wireOp",EDGE,"E36.0.11.0"),sQuery(id+"F6.wireOp",EDGE,"E36.0.12.0"),sQuery(id+"F6.wireOp",EDGE,"E36.0.13.0"),sQuery(id+"F6.wireOp",EDGE,"E36.0.14.0"),sQuery(id+"F6.wireOp",EDGE,"E36.0.15.0"),sQuery(id+"F6.wireOp",EDGE,"E36.0.16.0"),sQuery(id+"F6.wireOp",EDGE,"E36.0.17.0"),sQuery(id+"F6.wireOp",EDGE,"E36.0.18.0"),sQuery(id+"F6.wireOp",EDGE,"E36.0.19.0"),sQuery(id+"F6.wireOp",EDGE,"E36.1.0.0"),sQuery(id+"F6.wireOp",EDGE,"E36.1.1.0"),sQuery(id+"F6.wireOp",EDGE,"E36.1.2.0"),sQuery(id+"F6.wireOp",EDGE,"E36.1.3.0"),sQuery(id+"F6.wireOp",EDGE,"E36.1.4.0"),sQuery(id+"F6.wireOp",EDGE,"E36.1.5.0"),sQuery(id+"F6.wireOp",EDGE,"E36.1.6.0"),sQuery(id+"F6.wireOp",EDGE,"E36.1.7.0"),sQuery(id+"F6.wireOp",EDGE,"E36.1.8.0"),sQuery(id+"F6.wireOp",EDGE,"E36.1.9.0"),sQuery(id+"F6.wireOp",EDGE,"E36.1.10.0"),sQuery(id+"F6.wireOp",EDGE,"E36.1.11.0"),sQuery(id+"F6.wireOp",EDGE,"E36.1.12.0"),sQuery(id+"F6.wireOp",EDGE,"E36.1.13.0"),sQuery(id+"F6.wireOp",EDGE,"E36.1.14.0"),sQuery(id+"F6.wireOp",EDGE,"E36.1.15.0"),sQuery(id+"F6.wireOp",EDGE,"E36.1.16.0"),sQuery(id+"F6.wireOp",EDGE,"E36.1.17.0"),sQuery(id+"F6.wireOp",EDGE,"E36.1.18.0"),sQuery(id+"F6.wireOp",EDGE,"E36.1.19.0")])]});
            var Q2;
            Q2=qCreatedBy(makeId("Right.planeOp"),FACE);
            mirror(context, id + "F8", {"entities" : qUnion([Q0, Q1]), "mirrorPlane" : qUnion([Q2])});
        }
    });
